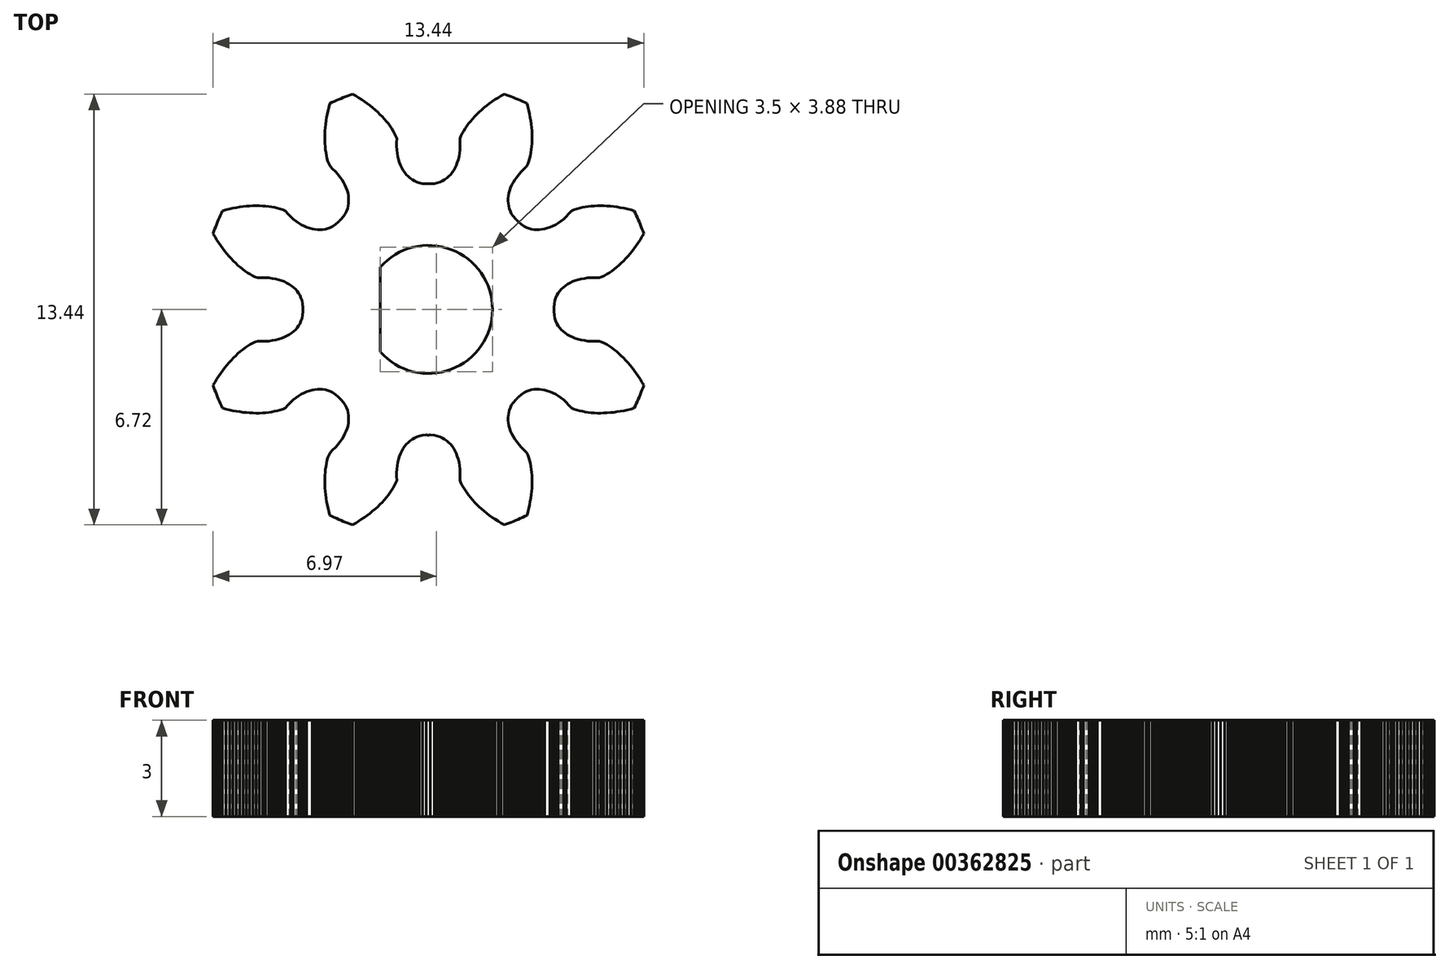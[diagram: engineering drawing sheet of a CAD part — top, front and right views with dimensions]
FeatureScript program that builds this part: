
annotation { "Feature Type Name" : "Feature", "Feature Type Description" : "" }
export const myFeature = defineFeature(function(context is Context, id is Id, definition is map)
    precondition{}
    {
        {
            var Q0;
            Q0=qCreatedBy(makeId("Top.planeOp"),FACE);
            var sketch = newSketch(context, id + "F0", { "sketchPlane" : qUnion([Q0])});
            skLineSegment(sketch, "E0", {"start": v(3.92, 0) * mm, "end": v(3.92, 0.01) * mm});
            skLineSegment(sketch, "E1", {"start": v(3.92, 0.01) * mm, "end": v(3.92, 0.03) * mm});
            skLineSegment(sketch, "E2", {"start": v(3.92, 0.03) * mm, "end": v(3.92, 0.04) * mm});
            skLineSegment(sketch, "E3", {"start": v(3.92, 0.04) * mm, "end": v(3.92, 0.05) * mm});
            skLineSegment(sketch, "E4", {"start": v(3.92, 0.05) * mm, "end": v(3.92, 0.06) * mm});
            skLineSegment(sketch, "E5", {"start": v(3.92, 0.06) * mm, "end": v(3.93, 0.18) * mm});
            skLineSegment(sketch, "E6", {"start": v(3.93, 0.18) * mm, "end": v(3.95, 0.28) * mm});
            skLineSegment(sketch, "E7", {"start": v(3.95, 0.28) * mm, "end": v(3.97, 0.36) * mm});
            skLineSegment(sketch, "E8", {"start": v(3.97, 0.36) * mm, "end": v(4, 0.44) * mm});
            skLineSegment(sketch, "E9", {"start": v(4, 0.44) * mm, "end": v(4.05, 0.5) * mm});
            skLineSegment(sketch, "E10", {"start": v(4.05, 0.5) * mm, "end": v(4.1, 0.57) * mm});
            skLineSegment(sketch, "E11", {"start": v(4.1, 0.57) * mm, "end": v(4.15, 0.63) * mm});
            skLineSegment(sketch, "E12", {"start": v(4.15, 0.63) * mm, "end": v(4.2, 0.69) * mm});
            skLineSegment(sketch, "E13", {"start": v(4.2, 0.69) * mm, "end": v(4.27, 0.74) * mm});
            skLineSegment(sketch, "E14", {"start": v(4.27, 0.74) * mm, "end": v(4.34, 0.79) * mm});
            skLineSegment(sketch, "E15", {"start": v(4.34, 0.79) * mm, "end": v(4.42, 0.83) * mm});
            skLineSegment(sketch, "E16", {"start": v(4.42, 0.83) * mm, "end": v(4.5, 0.87) * mm});
            skLineSegment(sketch, "E17", {"start": v(4.5, 0.87) * mm, "end": v(4.58, 0.9) * mm});
            skLineSegment(sketch, "E18", {"start": v(4.58, 0.9) * mm, "end": v(4.67, 0.93) * mm});
            skLineSegment(sketch, "E19", {"start": v(4.67, 0.93) * mm, "end": v(4.77, 0.96) * mm});
            skLineSegment(sketch, "E20", {"start": v(4.77, 0.96) * mm, "end": v(4.87, 0.97) * mm});
            skLineSegment(sketch, "E21", {"start": v(4.87, 0.97) * mm, "end": v(4.98, 0.99) * mm});
            skLineSegment(sketch, "E22", {"start": v(4.98, 0.99) * mm, "end": v(5.1, 1) * mm});
            skLineSegment(sketch, "E23", {"start": v(5.1, 1) * mm, "end": v(5.2, 0.99) * mm});
            skLineSegment(sketch, "E24", {"start": v(5.2, 0.99) * mm, "end": v(5.33, 0.99) * mm});
            skLineSegment(sketch, "E25", {"start": v(5.33, 0.99) * mm, "end": v(5.41, 1.02) * mm});
            skLineSegment(sketch, "E26", {"start": v(5.41, 1.02) * mm, "end": v(5.49, 1.06) * mm});
            skLineSegment(sketch, "E27", {"start": v(5.49, 1.06) * mm, "end": v(5.57, 1.1) * mm});
            skLineSegment(sketch, "E28", {"start": v(5.57, 1.1) * mm, "end": v(5.65, 1.15) * mm});
            skLineSegment(sketch, "E29", {"start": v(5.65, 1.15) * mm, "end": v(5.72, 1.2) * mm});
            skLineSegment(sketch, "E30", {"start": v(5.72, 1.2) * mm, "end": v(5.8, 1.25) * mm});
            skLineSegment(sketch, "E31", {"start": v(5.8, 1.25) * mm, "end": v(5.87, 1.31) * mm});
            skLineSegment(sketch, "E32", {"start": v(5.87, 1.31) * mm, "end": v(5.94, 1.38) * mm});
            skLineSegment(sketch, "E33", {"start": v(5.94, 1.38) * mm, "end": v(6.02, 1.44) * mm});
            skLineSegment(sketch, "E34", {"start": v(6.02, 1.44) * mm, "end": v(6.09, 1.51) * mm});
            skLineSegment(sketch, "E35", {"start": v(6.09, 1.51) * mm, "end": v(6.16, 1.58) * mm});
            skLineSegment(sketch, "E36", {"start": v(6.16, 1.58) * mm, "end": v(6.23, 1.66) * mm});
            skLineSegment(sketch, "E37", {"start": v(6.23, 1.66) * mm, "end": v(6.3, 1.74) * mm});
            skLineSegment(sketch, "E38", {"start": v(6.3, 1.74) * mm, "end": v(6.36, 1.82) * mm});
            skLineSegment(sketch, "E39", {"start": v(6.36, 1.82) * mm, "end": v(6.42, 1.9) * mm});
            skLineSegment(sketch, "E40", {"start": v(6.42, 1.9) * mm, "end": v(6.48, 2) * mm});
            skLineSegment(sketch, "E41", {"start": v(6.48, 2) * mm, "end": v(6.55, 2.08) * mm});
            skLineSegment(sketch, "E42", {"start": v(6.55, 2.08) * mm, "end": v(6.6, 2.17) * mm});
            skLineSegment(sketch, "E43", {"start": v(6.6, 2.17) * mm, "end": v(6.66, 2.27) * mm});
            skLineSegment(sketch, "E44", {"start": v(6.66, 2.27) * mm, "end": v(6.72, 2.37) * mm});
            skLineSegment(sketch, "E45", {"start": v(6.72, 2.37) * mm, "end": v(6.7, 2.44) * mm});
            skLineSegment(sketch, "E46", {"start": v(6.7, 2.44) * mm, "end": v(6.67, 2.51) * mm});
            skLineSegment(sketch, "E47", {"start": v(6.67, 2.51) * mm, "end": v(6.64, 2.58) * mm});
            skLineSegment(sketch, "E48", {"start": v(6.64, 2.58) * mm, "end": v(6.61, 2.66) * mm});
            skLineSegment(sketch, "E49", {"start": v(6.61, 2.66) * mm, "end": v(6.58, 2.73) * mm});
            skPoint(sketch, "E50", {"position": v(0, 5.7) * mm});
            skPoint(sketch, "E51", {"position": v(5.7, 0) * mm});
            skPoint(sketch, "E52", {"position": v(0, 0) * mm});
            skPoint(sketch, "E53", {"position": v(0, -5.7) * mm});
            skCircle(sketch, "E54", {"center": v(0, 0) * mm, "radius": 5.7 * mm, "construction": true});
            skLineSegment(sketch, "E55", {"start": v(5.7, 0) * mm, "end": v(-5.7, 0) * mm, "construction": true});
            skLineSegment(sketch, "E56", {"start": v(0, 5.7) * mm, "end": v(0, -5.7) * mm, "construction": true});
            skLineSegment(sketch, "E57.MirrorCS", {"start": v(3.92, 0) * mm, "end": v(3.92, -0.01) * mm});
            skLineSegment(sketch, "E58.MirrorCS", {"start": v(3.92, -0.03) * mm, "end": v(3.92, -0.04) * mm});
            skLineSegment(sketch, "E59.MirrorCS", {"start": v(3.92, -0.05) * mm, "end": v(3.92, -0.06) * mm});
            skLineSegment(sketch, "E60.MirrorCS", {"start": v(3.92, -0.01) * mm, "end": v(3.92, -0.03) * mm});
            skLineSegment(sketch, "E61.MirrorCS", {"start": v(3.92, -0.04) * mm, "end": v(3.92, -0.05) * mm});
            skLineSegment(sketch, "E62.MirrorCS", {"start": v(6.09, -1.51) * mm, "end": v(6.16, -1.58) * mm});
            skLineSegment(sketch, "E63.MirrorCS", {"start": v(4.67, -0.93) * mm, "end": v(4.77, -0.96) * mm});
            skLineSegment(sketch, "E64.MirrorCS", {"start": v(4.2, -0.69) * mm, "end": v(4.27, -0.74) * mm});
            skLineSegment(sketch, "E65.MirrorCS", {"start": v(4.27, -0.74) * mm, "end": v(4.34, -0.79) * mm});
            skLineSegment(sketch, "E66.MirrorCS", {"start": v(4.34, -0.79) * mm, "end": v(4.42, -0.83) * mm});
            skLineSegment(sketch, "E67.MirrorCS", {"start": v(3.92, -0.06) * mm, "end": v(3.93, -0.18) * mm});
            skLineSegment(sketch, "E68.MirrorCS", {"start": v(3.93, -0.18) * mm, "end": v(3.95, -0.28) * mm});
            skLineSegment(sketch, "E69.MirrorCS", {"start": v(3.95, -0.28) * mm, "end": v(3.97, -0.36) * mm});
            skLineSegment(sketch, "E70.MirrorCS", {"start": v(6.02, -1.44) * mm, "end": v(6.09, -1.51) * mm});
            skLineSegment(sketch, "E71.MirrorCS", {"start": v(3.97, -0.36) * mm, "end": v(4, -0.44) * mm});
            skLineSegment(sketch, "E72.MirrorCS", {"start": v(4, -0.44) * mm, "end": v(4.05, -0.5) * mm});
            skLineSegment(sketch, "E73.MirrorCS", {"start": v(4.05, -0.5) * mm, "end": v(4.1, -0.57) * mm});
            skLineSegment(sketch, "E74.MirrorCS", {"start": v(4.1, -0.57) * mm, "end": v(4.15, -0.63) * mm});
            skLineSegment(sketch, "E75.MirrorCS", {"start": v(4.15, -0.63) * mm, "end": v(4.2, -0.69) * mm});
            skLineSegment(sketch, "E76.MirrorCS", {"start": v(5.49, -1.06) * mm, "end": v(5.57, -1.1) * mm});
            skLineSegment(sketch, "E77.MirrorCS", {"start": v(6.6, -2.17) * mm, "end": v(6.66, -2.27) * mm});
            skLineSegment(sketch, "E78.MirrorCS", {"start": v(6.36, -1.82) * mm, "end": v(6.42, -1.9) * mm});
            skLineSegment(sketch, "E79.MirrorCS", {"start": v(5.1, -1) * mm, "end": v(5.2, -0.99) * mm});
            skLineSegment(sketch, "E80.MirrorCS", {"start": v(4.77, -0.96) * mm, "end": v(4.87, -0.97) * mm});
            skLineSegment(sketch, "E81.MirrorCS", {"start": v(6.72, -2.37) * mm, "end": v(6.7, -2.44) * mm});
            skLineSegment(sketch, "E82.MirrorCS", {"start": v(5.41, -1.02) * mm, "end": v(5.49, -1.06) * mm});
            skLineSegment(sketch, "E83.MirrorCS", {"start": v(5.65, -1.15) * mm, "end": v(5.72, -1.2) * mm});
            skLineSegment(sketch, "E84.MirrorCS", {"start": v(6.16, -1.58) * mm, "end": v(6.23, -1.66) * mm});
            skLineSegment(sketch, "E85.MirrorCS", {"start": v(4.42, -0.83) * mm, "end": v(4.5, -0.87) * mm});
            skLineSegment(sketch, "E86.MirrorCS", {"start": v(6.55, -2.08) * mm, "end": v(6.6, -2.17) * mm});
            skLineSegment(sketch, "E87.MirrorCS", {"start": v(6.64, -2.58) * mm, "end": v(6.61, -2.66) * mm});
            skLineSegment(sketch, "E88.MirrorCS", {"start": v(5.87, -1.31) * mm, "end": v(5.94, -1.38) * mm});
            skLineSegment(sketch, "E89.MirrorCS", {"start": v(6.66, -2.27) * mm, "end": v(6.72, -2.37) * mm});
            skLineSegment(sketch, "E90.MirrorCS", {"start": v(5.57, -1.1) * mm, "end": v(5.65, -1.15) * mm});
            skLineSegment(sketch, "E91.MirrorCS", {"start": v(6.42, -1.9) * mm, "end": v(6.48, -2) * mm});
            skLineSegment(sketch, "E92.MirrorCS", {"start": v(5.2, -0.99) * mm, "end": v(5.33, -0.99) * mm});
            skLineSegment(sketch, "E93.MirrorCS", {"start": v(4.87, -0.97) * mm, "end": v(4.98, -0.99) * mm});
            skLineSegment(sketch, "E94.MirrorCS", {"start": v(6.7, -2.44) * mm, "end": v(6.67, -2.51) * mm});
            skLineSegment(sketch, "E95.MirrorCS", {"start": v(5.72, -1.2) * mm, "end": v(5.8, -1.25) * mm});
            skLineSegment(sketch, "E96.MirrorCS", {"start": v(4.58, -0.9) * mm, "end": v(4.67, -0.93) * mm});
            skLineSegment(sketch, "E97.MirrorCS", {"start": v(6.23, -1.66) * mm, "end": v(6.3, -1.74) * mm});
            skLineSegment(sketch, "E98.MirrorCS", {"start": v(4.5, -0.87) * mm, "end": v(4.58, -0.9) * mm});
            skLineSegment(sketch, "E99.MirrorCS", {"start": v(6.61, -2.66) * mm, "end": v(6.58, -2.73) * mm});
            skLineSegment(sketch, "E100.MirrorCS", {"start": v(5.94, -1.38) * mm, "end": v(6.02, -1.44) * mm});
            skLineSegment(sketch, "E101.MirrorCS", {"start": v(6.48, -2) * mm, "end": v(6.55, -2.08) * mm});
            skLineSegment(sketch, "E102.MirrorCS", {"start": v(5.33, -0.99) * mm, "end": v(5.41, -1.02) * mm});
            skLineSegment(sketch, "E103.MirrorCS", {"start": v(6.67, -2.51) * mm, "end": v(6.64, -2.58) * mm});
            skLineSegment(sketch, "E104.MirrorCS", {"start": v(4.98, -0.99) * mm, "end": v(5.1, -1) * mm});
            skLineSegment(sketch, "E105.MirrorCS", {"start": v(6.3, -1.74) * mm, "end": v(6.36, -1.82) * mm});
            skLineSegment(sketch, "E106.MirrorCS", {"start": v(5.8, -1.25) * mm, "end": v(5.87, -1.31) * mm});
            skPoint(sketch, "E107.1.0", {"position": v(4.03, 4.03) * mm});
            skPoint(sketch, "E107.1.1", {"position": v(4.03, 4.03) * mm});
            skLineSegment(sketch, "E107.1.2", {"start": v(4.22, 2.82) * mm, "end": v(4.3, 2.9) * mm});
            skLineSegment(sketch, "E107.1.3", {"start": v(5.58, 3.23) * mm, "end": v(5.68, 3.22) * mm});
            skLineSegment(sketch, "E107.1.4", {"start": v(5.37, 3.23) * mm, "end": v(5.47, 3.23) * mm});
            skLineSegment(sketch, "E107.1.5", {"start": v(3.16, 6.1) * mm, "end": v(3.13, 6.2) * mm});
            skLineSegment(sketch, "E107.1.6", {"start": v(3.1, 4.54) * mm, "end": v(3.14, 4.63) * mm});
            skLineSegment(sketch, "E107.1.7", {"start": v(5.78, 3.2) * mm, "end": v(5.89, 3.2) * mm});
            skLineSegment(sketch, "E107.1.8", {"start": v(2.65, 3.96) * mm, "end": v(2.7, 4.05) * mm});
            skLineSegment(sketch, "E107.1.9", {"start": v(3.06, 2.56) * mm, "end": v(3.15, 2.52) * mm});
            skLineSegment(sketch, "E107.1.10", {"start": v(4.8, 3.18) * mm, "end": v(4.9, 3.2) * mm});
            skLineSegment(sketch, "E107.1.11", {"start": v(3.23, 5.37) * mm, "end": v(3.23, 5.47) * mm});
            skLineSegment(sketch, "E107.1.12", {"start": v(3.1, 6.32) * mm, "end": v(3.08, 6.43) * mm});
            skLineSegment(sketch, "E107.1.13", {"start": v(3.46, 2.49) * mm, "end": v(3.54, 2.5) * mm});
            skLineSegment(sketch, "E107.1.14", {"start": v(3.16, 4.71) * mm, "end": v(3.18, 4.8) * mm});
            skLineSegment(sketch, "E107.1.15", {"start": v(4.05, 2.7) * mm, "end": v(4.13, 2.76) * mm});
            skLineSegment(sketch, "E107.1.16", {"start": v(3.88, 2.6) * mm, "end": v(3.96, 2.65) * mm});
            skLineSegment(sketch, "E107.1.17", {"start": v(4.54, 3.1) * mm, "end": v(4.63, 3.14) * mm});
            skLineSegment(sketch, "E107.1.18", {"start": v(3.63, 2.51) * mm, "end": v(3.71, 2.54) * mm});
            skLineSegment(sketch, "E107.1.19", {"start": v(6.32, 3.1) * mm, "end": v(6.43, 3.08) * mm});
            skLineSegment(sketch, "E107.1.20", {"start": v(3.22, 2.5) * mm, "end": v(3.3, 2.5) * mm});
            skLineSegment(sketch, "E107.1.21", {"start": v(3.23, 5.58) * mm, "end": v(3.22, 5.68) * mm});
            skLineSegment(sketch, "E107.1.22", {"start": v(3.2, 4.9) * mm, "end": v(3.21, 4.99) * mm});
            skLineSegment(sketch, "E107.1.23", {"start": v(4.71, 3.16) * mm, "end": v(4.8, 3.18) * mm});
            skLineSegment(sketch, "E107.1.24", {"start": v(3.96, 2.65) * mm, "end": v(4.05, 2.7) * mm});
            skLineSegment(sketch, "E107.1.25", {"start": v(3.13, 6.2) * mm, "end": v(3.1, 6.32) * mm});
            skLineSegment(sketch, "E107.1.26", {"start": v(4.9, 3.2) * mm, "end": v(4.99, 3.21) * mm});
            skLineSegment(sketch, "E107.1.27", {"start": v(3.14, 4.63) * mm, "end": v(3.16, 4.71) * mm});
            skLineSegment(sketch, "E107.1.28", {"start": v(2.7, 4.05) * mm, "end": v(2.76, 4.13) * mm});
            skLineSegment(sketch, "E107.1.29", {"start": v(4.3, 2.9) * mm, "end": v(4.38, 2.98) * mm});
            skLineSegment(sketch, "E107.1.30", {"start": v(5.08, 3.22) * mm, "end": v(5.18, 3.23) * mm});
            skLineSegment(sketch, "E107.1.31", {"start": v(5.68, 3.22) * mm, "end": v(5.78, 3.2) * mm});
            skLineSegment(sketch, "E107.1.32", {"start": v(3.8, 2.57) * mm, "end": v(3.88, 2.6) * mm});
            skLineSegment(sketch, "E107.1.33", {"start": v(3.15, 2.52) * mm, "end": v(3.22, 2.5) * mm});
            skLineSegment(sketch, "E107.1.34", {"start": v(3.54, 2.5) * mm, "end": v(3.63, 2.51) * mm});
            skLineSegment(sketch, "E107.1.35", {"start": v(3.23, 5.47) * mm, "end": v(3.23, 5.58) * mm});
            skLineSegment(sketch, "E107.1.36", {"start": v(3.18, 4.8) * mm, "end": v(3.2, 4.9) * mm});
            skLineSegment(sketch, "E107.1.37", {"start": v(3.3, 2.5) * mm, "end": v(3.38, 2.49) * mm});
            skLineSegment(sketch, "E107.1.38", {"start": v(3.22, 5.68) * mm, "end": v(3.2, 5.78) * mm});
            skLineSegment(sketch, "E107.1.39", {"start": v(3.21, 4.99) * mm, "end": v(3.22, 5.08) * mm});
            skLineSegment(sketch, "E107.1.40", {"start": v(4.99, 3.21) * mm, "end": v(5.08, 3.22) * mm});
            skLineSegment(sketch, "E107.1.41", {"start": v(6.55, 2.8) * mm, "end": v(6.58, 2.73) * mm});
            skLineSegment(sketch, "E107.1.42", {"start": v(2.49, 3.46) * mm, "end": v(2.5, 3.54) * mm});
            skLineSegment(sketch, "E107.1.43", {"start": v(2.5, 3.54) * mm, "end": v(2.51, 3.63) * mm});
            skLineSegment(sketch, "E107.1.44", {"start": v(2.51, 3.63) * mm, "end": v(2.54, 3.71) * mm});
            skLineSegment(sketch, "E107.1.45", {"start": v(2.65, 2.9) * mm, "end": v(2.6, 2.99) * mm});
            skLineSegment(sketch, "E107.1.46", {"start": v(2.6, 2.99) * mm, "end": v(2.56, 3.06) * mm});
            skLineSegment(sketch, "E107.1.47", {"start": v(2.56, 3.06) * mm, "end": v(2.52, 3.15) * mm});
            skLineSegment(sketch, "E107.1.48", {"start": v(2.52, 3.15) * mm, "end": v(2.5, 3.22) * mm});
            skLineSegment(sketch, "E107.1.49", {"start": v(2.5, 3.22) * mm, "end": v(2.5, 3.3) * mm});
            skLineSegment(sketch, "E107.1.50", {"start": v(2.5, 3.3) * mm, "end": v(2.49, 3.38) * mm});
            skLineSegment(sketch, "E107.1.51", {"start": v(2.49, 3.38) * mm, "end": v(2.49, 3.46) * mm});
            skLineSegment(sketch, "E107.1.52", {"start": v(5.18, 3.23) * mm, "end": v(5.27, 3.23) * mm});
            skLineSegment(sketch, "E107.1.53", {"start": v(3.2, 5.78) * mm, "end": v(3.2, 5.89) * mm});
            skLineSegment(sketch, "E107.1.54", {"start": v(5.89, 3.2) * mm, "end": v(6, 3.18) * mm});
            skLineSegment(sketch, "E107.1.55", {"start": v(3.38, 2.49) * mm, "end": v(3.46, 2.49) * mm});
            skLineSegment(sketch, "E107.1.56", {"start": v(2.54, 3.71) * mm, "end": v(2.57, 3.8) * mm});
            skLineSegment(sketch, "E107.1.57", {"start": v(5.47, 3.23) * mm, "end": v(5.58, 3.23) * mm});
            skLineSegment(sketch, "E107.1.58", {"start": v(3.22, 5.08) * mm, "end": v(3.23, 5.18) * mm});
            skLineSegment(sketch, "E107.1.59", {"start": v(3.2, 5.89) * mm, "end": v(3.18, 6) * mm});
            skLineSegment(sketch, "E107.1.60", {"start": v(2.98, 4.38) * mm, "end": v(3.07, 4.47) * mm});
            skLineSegment(sketch, "E107.1.61", {"start": v(4.38, 2.98) * mm, "end": v(4.47, 3.07) * mm});
            skLineSegment(sketch, "E107.1.62", {"start": v(4.63, 3.14) * mm, "end": v(4.71, 3.16) * mm});
            skLineSegment(sketch, "E107.1.63", {"start": v(2.57, 3.8) * mm, "end": v(2.6, 3.88) * mm});
            skLineSegment(sketch, "E107.1.64", {"start": v(3.71, 2.54) * mm, "end": v(3.8, 2.57) * mm});
            skLineSegment(sketch, "E107.1.65", {"start": v(3.23, 5.18) * mm, "end": v(3.23, 5.27) * mm});
            skLineSegment(sketch, "E107.1.66", {"start": v(6, 3.18) * mm, "end": v(6.1, 3.16) * mm});
            skLineSegment(sketch, "E107.1.67", {"start": v(3.18, 6) * mm, "end": v(3.16, 6.1) * mm});
            skLineSegment(sketch, "E107.1.68", {"start": v(3.07, 4.47) * mm, "end": v(3.1, 4.54) * mm});
            skLineSegment(sketch, "E107.1.69", {"start": v(4.13, 2.76) * mm, "end": v(4.22, 2.82) * mm});
            skLineSegment(sketch, "E107.1.70", {"start": v(6.2, 3.13) * mm, "end": v(6.32, 3.1) * mm});
            skLineSegment(sketch, "E107.1.71", {"start": v(2.6, 3.88) * mm, "end": v(2.65, 3.96) * mm});
            skLineSegment(sketch, "E107.1.72", {"start": v(6.1, 3.16) * mm, "end": v(6.2, 3.13) * mm});
            skLineSegment(sketch, "E107.1.73", {"start": v(5.27, 3.23) * mm, "end": v(5.37, 3.23) * mm});
            skLineSegment(sketch, "E107.1.74", {"start": v(3.23, 5.27) * mm, "end": v(3.23, 5.37) * mm});
            skLineSegment(sketch, "E107.1.75", {"start": v(4.47, 3.07) * mm, "end": v(4.54, 3.1) * mm});
            skLineSegment(sketch, "E107.1.76", {"start": v(2.76, 4.13) * mm, "end": v(2.82, 4.22) * mm});
            skLineSegment(sketch, "E107.1.77", {"start": v(2.82, 4.22) * mm, "end": v(2.9, 4.3) * mm});
            skLineSegment(sketch, "E107.1.78", {"start": v(2.9, 4.3) * mm, "end": v(2.98, 4.38) * mm});
            skLineSegment(sketch, "E107.1.79", {"start": v(2.8, 6.55) * mm, "end": v(2.73, 6.58) * mm});
            skLineSegment(sketch, "E107.1.80", {"start": v(6.46, 3) * mm, "end": v(6.5, 2.94) * mm});
            skLineSegment(sketch, "E107.1.81", {"start": v(6.52, 2.87) * mm, "end": v(6.55, 2.8) * mm});
            skLineSegment(sketch, "E107.1.82", {"start": v(6.5, 2.94) * mm, "end": v(6.52, 2.87) * mm});
            skLineSegment(sketch, "E107.1.83", {"start": v(3, 6.46) * mm, "end": v(2.94, 6.5) * mm});
            skLineSegment(sketch, "E107.1.84", {"start": v(6.43, 3.08) * mm, "end": v(6.46, 3) * mm});
            skLineSegment(sketch, "E107.1.85", {"start": v(3.08, 6.43) * mm, "end": v(3, 6.46) * mm});
            skLineSegment(sketch, "E107.1.86", {"start": v(2.94, 6.5) * mm, "end": v(2.87, 6.52) * mm});
            skLineSegment(sketch, "E107.1.87", {"start": v(2.9, 2.65) * mm, "end": v(2.99, 2.6) * mm});
            skLineSegment(sketch, "E107.1.88", {"start": v(2.87, 6.52) * mm, "end": v(2.8, 6.55) * mm});
            skLineSegment(sketch, "E107.1.89", {"start": v(2.99, 2.6) * mm, "end": v(3.06, 2.56) * mm});
            skLineSegment(sketch, "E107.1.90", {"start": v(2.82, 2.73) * mm, "end": v(2.9, 2.65) * mm});
            skLineSegment(sketch, "E107.1.91", {"start": v(2.79, 2.75) * mm, "end": v(2.8, 2.74) * mm});
            skLineSegment(sketch, "E107.1.92", {"start": v(2.76, 2.78) * mm, "end": v(2.75, 2.79) * mm});
            skLineSegment(sketch, "E107.1.93", {"start": v(2.73, 2.82) * mm, "end": v(2.65, 2.9) * mm});
            skLineSegment(sketch, "E107.1.94", {"start": v(2.74, 2.8) * mm, "end": v(2.73, 2.82) * mm});
            skLineSegment(sketch, "E107.1.95", {"start": v(2.74, 2.8) * mm, "end": v(2.74, 2.8) * mm});
            skLineSegment(sketch, "E107.1.96", {"start": v(2.75, 2.79) * mm, "end": v(2.74, 2.8) * mm});
            skLineSegment(sketch, "E107.1.97", {"start": v(2.77, 2.77) * mm, "end": v(2.76, 2.78) * mm});
            skLineSegment(sketch, "E107.1.98", {"start": v(2.77, 2.77) * mm, "end": v(2.78, 2.76) * mm});
            skLineSegment(sketch, "E107.1.99", {"start": v(2.78, 2.76) * mm, "end": v(2.79, 2.75) * mm});
            skLineSegment(sketch, "E107.1.100", {"start": v(2.8, 2.74) * mm, "end": v(2.8, 2.74) * mm});
            skLineSegment(sketch, "E107.1.101", {"start": v(2.8, 2.74) * mm, "end": v(2.82, 2.73) * mm});
            skLineSegment(sketch, "E107.2.2", {"start": v(0.99, 4.98) * mm, "end": v(1, 5.1) * mm});
            skLineSegment(sketch, "E107.2.3", {"start": v(1.66, 6.23) * mm, "end": v(1.74, 6.3) * mm});
            skLineSegment(sketch, "E107.2.4", {"start": v(1.51, 6.09) * mm, "end": v(1.58, 6.16) * mm});
            skLineSegment(sketch, "E107.2.5", {"start": v(-2.08, 6.55) * mm, "end": v(-2.17, 6.6) * mm});
            skLineSegment(sketch, "E107.2.6", {"start": v(-1.02, 5.41) * mm, "end": v(-1.06, 5.49) * mm});
            skLineSegment(sketch, "E107.2.7", {"start": v(1.82, 6.36) * mm, "end": v(1.9, 6.42) * mm});
            skLineSegment(sketch, "E107.2.8", {"start": v(-0.93, 4.67) * mm, "end": v(-0.96, 4.77) * mm});
            skLineSegment(sketch, "E107.2.9", {"start": v(0.36, 3.97) * mm, "end": v(0.44, 4) * mm});
            skLineSegment(sketch, "E107.2.10", {"start": v(1.15, 5.65) * mm, "end": v(1.2, 5.72) * mm});
            skLineSegment(sketch, "E107.2.11", {"start": v(-1.51, 6.09) * mm, "end": v(-1.58, 6.16) * mm});
            skLineSegment(sketch, "E107.2.12", {"start": v(-2.27, 6.66) * mm, "end": v(-2.37, 6.72) * mm});
            skLineSegment(sketch, "E107.2.13", {"start": v(0.69, 4.2) * mm, "end": v(0.74, 4.27) * mm});
            skLineSegment(sketch, "E107.2.14", {"start": v(-1.1, 5.57) * mm, "end": v(-1.15, 5.65) * mm});
            skLineSegment(sketch, "E107.2.15", {"start": v(0.96, 4.77) * mm, "end": v(0.97, 4.87) * mm});
            skLineSegment(sketch, "E107.2.16", {"start": v(0.9, 4.58) * mm, "end": v(0.93, 4.67) * mm});
            skLineSegment(sketch, "E107.2.17", {"start": v(1.02, 5.41) * mm, "end": v(1.06, 5.49) * mm});
            skLineSegment(sketch, "E107.2.18", {"start": v(0.79, 4.34) * mm, "end": v(0.83, 4.42) * mm});
            skLineSegment(sketch, "E107.2.19", {"start": v(2.27, 6.66) * mm, "end": v(2.37, 6.72) * mm});
            skLineSegment(sketch, "E107.2.20", {"start": v(0.5, 4.05) * mm, "end": v(0.57, 4.1) * mm});
            skLineSegment(sketch, "E107.2.21", {"start": v(-1.66, 6.23) * mm, "end": v(-1.74, 6.3) * mm});
            skLineSegment(sketch, "E107.2.22", {"start": v(-1.2, 5.72) * mm, "end": v(-1.25, 5.8) * mm});
            skLineSegment(sketch, "E107.2.23", {"start": v(1.1, 5.57) * mm, "end": v(1.15, 5.65) * mm});
            skLineSegment(sketch, "E107.2.24", {"start": v(0.93, 4.67) * mm, "end": v(0.96, 4.77) * mm});
            skLineSegment(sketch, "E107.2.25", {"start": v(-2.17, 6.6) * mm, "end": v(-2.27, 6.66) * mm});
            skLineSegment(sketch, "E107.2.26", {"start": v(1.2, 5.72) * mm, "end": v(1.25, 5.8) * mm});
            skLineSegment(sketch, "E107.2.27", {"start": v(-1.06, 5.49) * mm, "end": v(-1.1, 5.57) * mm});
            skLineSegment(sketch, "E107.2.28", {"start": v(-0.96, 4.77) * mm, "end": v(-0.97, 4.87) * mm});
            skLineSegment(sketch, "E107.2.29", {"start": v(1, 5.1) * mm, "end": v(0.99, 5.2) * mm});
            skLineSegment(sketch, "E107.2.30", {"start": v(1.31, 5.87) * mm, "end": v(1.38, 5.94) * mm});
            skLineSegment(sketch, "E107.2.31", {"start": v(1.74, 6.3) * mm, "end": v(1.82, 6.36) * mm});
            skLineSegment(sketch, "E107.2.32", {"start": v(0.87, 4.5) * mm, "end": v(0.9, 4.58) * mm});
            skLineSegment(sketch, "E107.2.33", {"start": v(0.44, 4) * mm, "end": v(0.5, 4.05) * mm});
            skLineSegment(sketch, "E107.2.34", {"start": v(0.74, 4.27) * mm, "end": v(0.79, 4.34) * mm});
            skLineSegment(sketch, "E107.2.35", {"start": v(-1.58, 6.16) * mm, "end": v(-1.66, 6.23) * mm});
            skLineSegment(sketch, "E107.2.36", {"start": v(-1.15, 5.65) * mm, "end": v(-1.2, 5.72) * mm});
            skLineSegment(sketch, "E107.2.37", {"start": v(0.57, 4.1) * mm, "end": v(0.63, 4.15) * mm});
            skLineSegment(sketch, "E107.2.38", {"start": v(-1.74, 6.3) * mm, "end": v(-1.82, 6.36) * mm});
            skLineSegment(sketch, "E107.2.39", {"start": v(-1.25, 5.8) * mm, "end": v(-1.31, 5.87) * mm});
            skLineSegment(sketch, "E107.2.40", {"start": v(1.25, 5.8) * mm, "end": v(1.31, 5.87) * mm});
            skLineSegment(sketch, "E107.2.41", {"start": v(2.66, 6.61) * mm, "end": v(2.73, 6.58) * mm});
            skLineSegment(sketch, "E107.2.42", {"start": v(-0.69, 4.2) * mm, "end": v(-0.74, 4.27) * mm});
            skLineSegment(sketch, "E107.2.43", {"start": v(-0.74, 4.27) * mm, "end": v(-0.79, 4.34) * mm});
            skLineSegment(sketch, "E107.2.44", {"start": v(-0.79, 4.34) * mm, "end": v(-0.83, 4.42) * mm});
            skLineSegment(sketch, "E107.2.45", {"start": v(-0.18, 3.93) * mm, "end": v(-0.28, 3.95) * mm});
            skLineSegment(sketch, "E107.2.46", {"start": v(-0.28, 3.95) * mm, "end": v(-0.36, 3.97) * mm});
            skLineSegment(sketch, "E107.2.47", {"start": v(-0.36, 3.97) * mm, "end": v(-0.44, 4) * mm});
            skLineSegment(sketch, "E107.2.48", {"start": v(-0.44, 4) * mm, "end": v(-0.5, 4.05) * mm});
            skLineSegment(sketch, "E107.2.49", {"start": v(-0.5, 4.05) * mm, "end": v(-0.57, 4.1) * mm});
            skLineSegment(sketch, "E107.2.50", {"start": v(-0.57, 4.1) * mm, "end": v(-0.63, 4.15) * mm});
            skLineSegment(sketch, "E107.2.51", {"start": v(-0.63, 4.15) * mm, "end": v(-0.69, 4.2) * mm});
            skLineSegment(sketch, "E107.2.52", {"start": v(1.38, 5.94) * mm, "end": v(1.44, 6.02) * mm});
            skLineSegment(sketch, "E107.2.53", {"start": v(-1.82, 6.36) * mm, "end": v(-1.9, 6.42) * mm});
            skLineSegment(sketch, "E107.2.54", {"start": v(1.9, 6.42) * mm, "end": v(2, 6.48) * mm});
            skLineSegment(sketch, "E107.2.55", {"start": v(0.63, 4.15) * mm, "end": v(0.69, 4.2) * mm});
            skLineSegment(sketch, "E107.2.56", {"start": v(-0.83, 4.42) * mm, "end": v(-0.87, 4.5) * mm});
            skLineSegment(sketch, "E107.2.57", {"start": v(1.58, 6.16) * mm, "end": v(1.66, 6.23) * mm});
            skLineSegment(sketch, "E107.2.58", {"start": v(-1.31, 5.87) * mm, "end": v(-1.38, 5.94) * mm});
            skLineSegment(sketch, "E107.2.59", {"start": v(-1.9, 6.42) * mm, "end": v(-2, 6.48) * mm});
            skLineSegment(sketch, "E107.2.60", {"start": v(-0.99, 5.2) * mm, "end": v(-0.99, 5.33) * mm});
            skLineSegment(sketch, "E107.2.61", {"start": v(0.99, 5.2) * mm, "end": v(0.99, 5.33) * mm});
            skLineSegment(sketch, "E107.2.62", {"start": v(1.06, 5.49) * mm, "end": v(1.1, 5.57) * mm});
            skLineSegment(sketch, "E107.2.63", {"start": v(-0.87, 4.5) * mm, "end": v(-0.9, 4.58) * mm});
            skLineSegment(sketch, "E107.2.64", {"start": v(0.83, 4.42) * mm, "end": v(0.87, 4.5) * mm});
            skLineSegment(sketch, "E107.2.65", {"start": v(-1.38, 5.94) * mm, "end": v(-1.44, 6.02) * mm});
            skLineSegment(sketch, "E107.2.66", {"start": v(2, 6.48) * mm, "end": v(2.08, 6.55) * mm});
            skLineSegment(sketch, "E107.2.67", {"start": v(-2, 6.48) * mm, "end": v(-2.08, 6.55) * mm});
            skLineSegment(sketch, "E107.2.68", {"start": v(-0.99, 5.33) * mm, "end": v(-1.02, 5.41) * mm});
            skLineSegment(sketch, "E107.2.69", {"start": v(0.97, 4.87) * mm, "end": v(0.99, 4.98) * mm});
            skLineSegment(sketch, "E107.2.70", {"start": v(2.17, 6.6) * mm, "end": v(2.27, 6.66) * mm});
            skLineSegment(sketch, "E107.2.71", {"start": v(-0.9, 4.58) * mm, "end": v(-0.93, 4.67) * mm});
            skLineSegment(sketch, "E107.2.72", {"start": v(2.08, 6.55) * mm, "end": v(2.17, 6.6) * mm});
            skLineSegment(sketch, "E107.2.73", {"start": v(1.44, 6.02) * mm, "end": v(1.51, 6.09) * mm});
            skLineSegment(sketch, "E107.2.74", {"start": v(-1.44, 6.02) * mm, "end": v(-1.51, 6.09) * mm});
            skLineSegment(sketch, "E107.2.75", {"start": v(0.99, 5.33) * mm, "end": v(1.02, 5.41) * mm});
            skLineSegment(sketch, "E107.2.76", {"start": v(-0.97, 4.87) * mm, "end": v(-0.99, 4.98) * mm});
            skLineSegment(sketch, "E107.2.77", {"start": v(-0.99, 4.98) * mm, "end": v(-1, 5.1) * mm});
            skLineSegment(sketch, "E107.2.78", {"start": v(-1, 5.1) * mm, "end": v(-0.99, 5.2) * mm});
            skLineSegment(sketch, "E107.2.79", {"start": v(-2.66, 6.61) * mm, "end": v(-2.73, 6.58) * mm});
            skLineSegment(sketch, "E107.2.80", {"start": v(2.44, 6.7) * mm, "end": v(2.51, 6.67) * mm});
            skLineSegment(sketch, "E107.2.81", {"start": v(2.58, 6.64) * mm, "end": v(2.66, 6.61) * mm});
            skLineSegment(sketch, "E107.2.82", {"start": v(2.51, 6.67) * mm, "end": v(2.58, 6.64) * mm});
            skLineSegment(sketch, "E107.2.83", {"start": v(-2.44, 6.7) * mm, "end": v(-2.51, 6.67) * mm});
            skLineSegment(sketch, "E107.2.84", {"start": v(2.37, 6.72) * mm, "end": v(2.44, 6.7) * mm});
            skLineSegment(sketch, "E107.2.85", {"start": v(-2.37, 6.72) * mm, "end": v(-2.44, 6.7) * mm});
            skLineSegment(sketch, "E107.2.86", {"start": v(-2.51, 6.67) * mm, "end": v(-2.58, 6.64) * mm});
            skLineSegment(sketch, "E107.2.87", {"start": v(0.18, 3.93) * mm, "end": v(0.28, 3.95) * mm});
            skLineSegment(sketch, "E107.2.88", {"start": v(-2.58, 6.64) * mm, "end": v(-2.66, 6.61) * mm});
            skLineSegment(sketch, "E107.2.89", {"start": v(0.28, 3.95) * mm, "end": v(0.36, 3.97) * mm});
            skLineSegment(sketch, "E107.2.90", {"start": v(0.06, 3.92) * mm, "end": v(0.18, 3.93) * mm});
            skLineSegment(sketch, "E107.2.91", {"start": v(0.03, 3.92) * mm, "end": v(0.04, 3.92) * mm});
            skLineSegment(sketch, "E107.2.92", {"start": v(-0.01, 3.92) * mm, "end": v(-0.03, 3.92) * mm});
            skLineSegment(sketch, "E107.2.93", {"start": v(-0.06, 3.92) * mm, "end": v(-0.18, 3.93) * mm});
            skLineSegment(sketch, "E107.2.94", {"start": v(-0.05, 3.92) * mm, "end": v(-0.06, 3.92) * mm});
            skLineSegment(sketch, "E107.2.95", {"start": v(-0.04, 3.92) * mm, "end": v(-0.05, 3.92) * mm});
            skLineSegment(sketch, "E107.2.96", {"start": v(-0.03, 3.92) * mm, "end": v(-0.04, 3.92) * mm});
            skLineSegment(sketch, "E107.2.97", {"start": v(0, 3.92) * mm, "end": v(-0.01, 3.92) * mm});
            skLineSegment(sketch, "E107.2.98", {"start": v(0, 3.92) * mm, "end": v(0.01, 3.92) * mm});
            skLineSegment(sketch, "E107.2.99", {"start": v(0.01, 3.92) * mm, "end": v(0.03, 3.92) * mm});
            skLineSegment(sketch, "E107.2.100", {"start": v(0.04, 3.92) * mm, "end": v(0.05, 3.92) * mm});
            skLineSegment(sketch, "E107.2.101", {"start": v(0.05, 3.92) * mm, "end": v(0.06, 3.92) * mm});
            skPoint(sketch, "E107.3.0", {"position": v(-4.03, 4.03) * mm});
            skPoint(sketch, "E107.3.1", {"position": v(-4.03, 4.03) * mm});
            skLineSegment(sketch, "E107.3.2", {"start": v(-2.82, 4.22) * mm, "end": v(-2.9, 4.3) * mm});
            skLineSegment(sketch, "E107.3.3", {"start": v(-3.23, 5.58) * mm, "end": v(-3.22, 5.68) * mm});
            skLineSegment(sketch, "E107.3.4", {"start": v(-3.23, 5.37) * mm, "end": v(-3.23, 5.47) * mm});
            skLineSegment(sketch, "E107.3.5", {"start": v(-6.1, 3.16) * mm, "end": v(-6.2, 3.13) * mm});
            skLineSegment(sketch, "E107.3.6", {"start": v(-4.54, 3.1) * mm, "end": v(-4.63, 3.14) * mm});
            skLineSegment(sketch, "E107.3.7", {"start": v(-3.2, 5.78) * mm, "end": v(-3.2, 5.89) * mm});
            skLineSegment(sketch, "E107.3.8", {"start": v(-3.96, 2.65) * mm, "end": v(-4.05, 2.7) * mm});
            skLineSegment(sketch, "E107.3.9", {"start": v(-2.56, 3.06) * mm, "end": v(-2.52, 3.15) * mm});
            skLineSegment(sketch, "E107.3.10", {"start": v(-3.18, 4.8) * mm, "end": v(-3.2, 4.9) * mm});
            skLineSegment(sketch, "E107.3.11", {"start": v(-5.37, 3.23) * mm, "end": v(-5.47, 3.23) * mm});
            skLineSegment(sketch, "E107.3.12", {"start": v(-6.32, 3.1) * mm, "end": v(-6.43, 3.08) * mm});
            skLineSegment(sketch, "E107.3.13", {"start": v(-2.49, 3.46) * mm, "end": v(-2.5, 3.54) * mm});
            skLineSegment(sketch, "E107.3.14", {"start": v(-4.71, 3.16) * mm, "end": v(-4.8, 3.18) * mm});
            skLineSegment(sketch, "E107.3.15", {"start": v(-2.7, 4.05) * mm, "end": v(-2.76, 4.13) * mm});
            skLineSegment(sketch, "E107.3.16", {"start": v(-2.6, 3.88) * mm, "end": v(-2.65, 3.96) * mm});
            skLineSegment(sketch, "E107.3.17", {"start": v(-3.1, 4.54) * mm, "end": v(-3.14, 4.63) * mm});
            skLineSegment(sketch, "E107.3.18", {"start": v(-2.51, 3.63) * mm, "end": v(-2.54, 3.71) * mm});
            skLineSegment(sketch, "E107.3.19", {"start": v(-3.1, 6.32) * mm, "end": v(-3.08, 6.43) * mm});
            skLineSegment(sketch, "E107.3.20", {"start": v(-2.5, 3.22) * mm, "end": v(-2.5, 3.3) * mm});
            skLineSegment(sketch, "E107.3.21", {"start": v(-5.58, 3.23) * mm, "end": v(-5.68, 3.22) * mm});
            skLineSegment(sketch, "E107.3.22", {"start": v(-4.9, 3.2) * mm, "end": v(-4.99, 3.21) * mm});
            skLineSegment(sketch, "E107.3.23", {"start": v(-3.16, 4.71) * mm, "end": v(-3.18, 4.8) * mm});
            skLineSegment(sketch, "E107.3.24", {"start": v(-2.65, 3.96) * mm, "end": v(-2.7, 4.05) * mm});
            skLineSegment(sketch, "E107.3.25", {"start": v(-6.2, 3.13) * mm, "end": v(-6.32, 3.1) * mm});
            skLineSegment(sketch, "E107.3.26", {"start": v(-3.2, 4.9) * mm, "end": v(-3.21, 4.99) * mm});
            skLineSegment(sketch, "E107.3.27", {"start": v(-4.63, 3.14) * mm, "end": v(-4.71, 3.16) * mm});
            skLineSegment(sketch, "E107.3.28", {"start": v(-4.05, 2.7) * mm, "end": v(-4.13, 2.76) * mm});
            skLineSegment(sketch, "E107.3.29", {"start": v(-2.9, 4.3) * mm, "end": v(-2.98, 4.38) * mm});
            skLineSegment(sketch, "E107.3.30", {"start": v(-3.22, 5.08) * mm, "end": v(-3.23, 5.18) * mm});
            skLineSegment(sketch, "E107.3.31", {"start": v(-3.22, 5.68) * mm, "end": v(-3.2, 5.78) * mm});
            skLineSegment(sketch, "E107.3.32", {"start": v(-2.57, 3.8) * mm, "end": v(-2.6, 3.88) * mm});
            skLineSegment(sketch, "E107.3.33", {"start": v(-2.52, 3.15) * mm, "end": v(-2.5, 3.22) * mm});
            skLineSegment(sketch, "E107.3.34", {"start": v(-2.5, 3.54) * mm, "end": v(-2.51, 3.63) * mm});
            skLineSegment(sketch, "E107.3.35", {"start": v(-5.47, 3.23) * mm, "end": v(-5.58, 3.23) * mm});
            skLineSegment(sketch, "E107.3.36", {"start": v(-4.8, 3.18) * mm, "end": v(-4.9, 3.2) * mm});
            skLineSegment(sketch, "E107.3.37", {"start": v(-2.5, 3.3) * mm, "end": v(-2.49, 3.38) * mm});
            skLineSegment(sketch, "E107.3.38", {"start": v(-5.68, 3.22) * mm, "end": v(-5.78, 3.2) * mm});
            skLineSegment(sketch, "E107.3.39", {"start": v(-4.99, 3.21) * mm, "end": v(-5.08, 3.22) * mm});
            skLineSegment(sketch, "E107.3.40", {"start": v(-3.21, 4.99) * mm, "end": v(-3.22, 5.08) * mm});
            skLineSegment(sketch, "E107.3.41", {"start": v(-2.8, 6.55) * mm, "end": v(-2.73, 6.58) * mm});
            skLineSegment(sketch, "E107.3.42", {"start": v(-3.46, 2.49) * mm, "end": v(-3.54, 2.5) * mm});
            skLineSegment(sketch, "E107.3.43", {"start": v(-3.54, 2.5) * mm, "end": v(-3.63, 2.51) * mm});
            skLineSegment(sketch, "E107.3.44", {"start": v(-3.63, 2.51) * mm, "end": v(-3.71, 2.54) * mm});
            skLineSegment(sketch, "E107.3.45", {"start": v(-2.9, 2.65) * mm, "end": v(-2.99, 2.6) * mm});
            skLineSegment(sketch, "E107.3.46", {"start": v(-2.99, 2.6) * mm, "end": v(-3.06, 2.56) * mm});
            skLineSegment(sketch, "E107.3.47", {"start": v(-3.06, 2.56) * mm, "end": v(-3.15, 2.52) * mm});
            skLineSegment(sketch, "E107.3.48", {"start": v(-3.15, 2.52) * mm, "end": v(-3.22, 2.5) * mm});
            skLineSegment(sketch, "E107.3.49", {"start": v(-3.22, 2.5) * mm, "end": v(-3.3, 2.5) * mm});
            skLineSegment(sketch, "E107.3.50", {"start": v(-3.3, 2.5) * mm, "end": v(-3.38, 2.49) * mm});
            skLineSegment(sketch, "E107.3.51", {"start": v(-3.38, 2.49) * mm, "end": v(-3.46, 2.49) * mm});
            skLineSegment(sketch, "E107.3.52", {"start": v(-3.23, 5.18) * mm, "end": v(-3.23, 5.27) * mm});
            skLineSegment(sketch, "E107.3.53", {"start": v(-5.78, 3.2) * mm, "end": v(-5.89, 3.2) * mm});
            skLineSegment(sketch, "E107.3.54", {"start": v(-3.2, 5.89) * mm, "end": v(-3.18, 6) * mm});
            skLineSegment(sketch, "E107.3.55", {"start": v(-2.49, 3.38) * mm, "end": v(-2.49, 3.46) * mm});
            skLineSegment(sketch, "E107.3.56", {"start": v(-3.71, 2.54) * mm, "end": v(-3.8, 2.57) * mm});
            skLineSegment(sketch, "E107.3.57", {"start": v(-3.23, 5.47) * mm, "end": v(-3.23, 5.58) * mm});
            skLineSegment(sketch, "E107.3.58", {"start": v(-5.08, 3.22) * mm, "end": v(-5.18, 3.23) * mm});
            skLineSegment(sketch, "E107.3.59", {"start": v(-5.89, 3.2) * mm, "end": v(-6, 3.18) * mm});
            skLineSegment(sketch, "E107.3.60", {"start": v(-4.38, 2.98) * mm, "end": v(-4.47, 3.07) * mm});
            skLineSegment(sketch, "E107.3.61", {"start": v(-2.98, 4.38) * mm, "end": v(-3.07, 4.47) * mm});
            skLineSegment(sketch, "E107.3.62", {"start": v(-3.14, 4.63) * mm, "end": v(-3.16, 4.71) * mm});
            skLineSegment(sketch, "E107.3.63", {"start": v(-3.8, 2.57) * mm, "end": v(-3.88, 2.6) * mm});
            skLineSegment(sketch, "E107.3.64", {"start": v(-2.54, 3.71) * mm, "end": v(-2.57, 3.8) * mm});
            skLineSegment(sketch, "E107.3.65", {"start": v(-5.18, 3.23) * mm, "end": v(-5.27, 3.23) * mm});
            skLineSegment(sketch, "E107.3.66", {"start": v(-3.18, 6) * mm, "end": v(-3.16, 6.1) * mm});
            skLineSegment(sketch, "E107.3.67", {"start": v(-6, 3.18) * mm, "end": v(-6.1, 3.16) * mm});
            skLineSegment(sketch, "E107.3.68", {"start": v(-4.47, 3.07) * mm, "end": v(-4.54, 3.1) * mm});
            skLineSegment(sketch, "E107.3.69", {"start": v(-2.76, 4.13) * mm, "end": v(-2.82, 4.22) * mm});
            skLineSegment(sketch, "E107.3.70", {"start": v(-3.13, 6.2) * mm, "end": v(-3.1, 6.32) * mm});
            skLineSegment(sketch, "E107.3.71", {"start": v(-3.88, 2.6) * mm, "end": v(-3.96, 2.65) * mm});
            skLineSegment(sketch, "E107.3.72", {"start": v(-3.16, 6.1) * mm, "end": v(-3.13, 6.2) * mm});
            skLineSegment(sketch, "E107.3.73", {"start": v(-3.23, 5.27) * mm, "end": v(-3.23, 5.37) * mm});
            skLineSegment(sketch, "E107.3.74", {"start": v(-5.27, 3.23) * mm, "end": v(-5.37, 3.23) * mm});
            skLineSegment(sketch, "E107.3.75", {"start": v(-3.07, 4.47) * mm, "end": v(-3.1, 4.54) * mm});
            skLineSegment(sketch, "E107.3.76", {"start": v(-4.13, 2.76) * mm, "end": v(-4.22, 2.82) * mm});
            skLineSegment(sketch, "E107.3.77", {"start": v(-4.22, 2.82) * mm, "end": v(-4.3, 2.9) * mm});
            skLineSegment(sketch, "E107.3.78", {"start": v(-4.3, 2.9) * mm, "end": v(-4.38, 2.98) * mm});
            skLineSegment(sketch, "E107.3.79", {"start": v(-6.55, 2.8) * mm, "end": v(-6.58, 2.73) * mm});
            skLineSegment(sketch, "E107.3.80", {"start": v(-3, 6.46) * mm, "end": v(-2.94, 6.5) * mm});
            skLineSegment(sketch, "E107.3.81", {"start": v(-2.87, 6.52) * mm, "end": v(-2.8, 6.55) * mm});
            skLineSegment(sketch, "E107.3.82", {"start": v(-2.94, 6.5) * mm, "end": v(-2.87, 6.52) * mm});
            skLineSegment(sketch, "E107.3.83", {"start": v(-6.46, 3) * mm, "end": v(-6.5, 2.94) * mm});
            skLineSegment(sketch, "E107.3.84", {"start": v(-3.08, 6.43) * mm, "end": v(-3, 6.46) * mm});
            skLineSegment(sketch, "E107.3.85", {"start": v(-6.43, 3.08) * mm, "end": v(-6.46, 3) * mm});
            skLineSegment(sketch, "E107.3.86", {"start": v(-6.5, 2.94) * mm, "end": v(-6.52, 2.87) * mm});
            skLineSegment(sketch, "E107.3.87", {"start": v(-2.65, 2.9) * mm, "end": v(-2.6, 2.99) * mm});
            skLineSegment(sketch, "E107.3.88", {"start": v(-6.52, 2.87) * mm, "end": v(-6.55, 2.8) * mm});
            skLineSegment(sketch, "E107.3.89", {"start": v(-2.6, 2.99) * mm, "end": v(-2.56, 3.06) * mm});
            skLineSegment(sketch, "E107.3.90", {"start": v(-2.73, 2.82) * mm, "end": v(-2.65, 2.9) * mm});
            skLineSegment(sketch, "E107.3.91", {"start": v(-2.75, 2.79) * mm, "end": v(-2.74, 2.8) * mm});
            skLineSegment(sketch, "E107.3.92", {"start": v(-2.78, 2.76) * mm, "end": v(-2.79, 2.75) * mm});
            skLineSegment(sketch, "E107.3.93", {"start": v(-2.82, 2.73) * mm, "end": v(-2.9, 2.65) * mm});
            skLineSegment(sketch, "E107.3.94", {"start": v(-2.8, 2.74) * mm, "end": v(-2.82, 2.73) * mm});
            skLineSegment(sketch, "E107.3.95", {"start": v(-2.8, 2.74) * mm, "end": v(-2.8, 2.74) * mm});
            skLineSegment(sketch, "E107.3.96", {"start": v(-2.79, 2.75) * mm, "end": v(-2.8, 2.74) * mm});
            skLineSegment(sketch, "E107.3.97", {"start": v(-2.77, 2.77) * mm, "end": v(-2.78, 2.76) * mm});
            skLineSegment(sketch, "E107.3.98", {"start": v(-2.77, 2.77) * mm, "end": v(-2.76, 2.78) * mm});
            skLineSegment(sketch, "E107.3.99", {"start": v(-2.76, 2.78) * mm, "end": v(-2.75, 2.79) * mm});
            skLineSegment(sketch, "E107.3.100", {"start": v(-2.74, 2.8) * mm, "end": v(-2.74, 2.8) * mm});
            skLineSegment(sketch, "E107.3.101", {"start": v(-2.74, 2.8) * mm, "end": v(-2.73, 2.82) * mm});
            skPoint(sketch, "E107.4.0", {"position": v(-5.7, 0) * mm});
            skPoint(sketch, "E107.4.1", {"position": v(-5.7, 0) * mm});
            skLineSegment(sketch, "E107.4.2", {"start": v(-4.98, 0.99) * mm, "end": v(-5.1, 1) * mm});
            skLineSegment(sketch, "E107.4.3", {"start": v(-6.23, 1.66) * mm, "end": v(-6.3, 1.74) * mm});
            skLineSegment(sketch, "E107.4.4", {"start": v(-6.09, 1.51) * mm, "end": v(-6.16, 1.58) * mm});
            skLineSegment(sketch, "E107.4.5", {"start": v(-6.55, -2.08) * mm, "end": v(-6.6, -2.17) * mm});
            skLineSegment(sketch, "E107.4.6", {"start": v(-5.41, -1.02) * mm, "end": v(-5.49, -1.06) * mm});
            skLineSegment(sketch, "E107.4.7", {"start": v(-6.36, 1.82) * mm, "end": v(-6.42, 1.9) * mm});
            skLineSegment(sketch, "E107.4.8", {"start": v(-4.67, -0.93) * mm, "end": v(-4.77, -0.96) * mm});
            skLineSegment(sketch, "E107.4.9", {"start": v(-3.97, 0.36) * mm, "end": v(-4, 0.44) * mm});
            skLineSegment(sketch, "E107.4.10", {"start": v(-5.65, 1.15) * mm, "end": v(-5.72, 1.2) * mm});
            skLineSegment(sketch, "E107.4.11", {"start": v(-6.09, -1.51) * mm, "end": v(-6.16, -1.58) * mm});
            skLineSegment(sketch, "E107.4.12", {"start": v(-6.66, -2.27) * mm, "end": v(-6.72, -2.37) * mm});
            skLineSegment(sketch, "E107.4.13", {"start": v(-4.2, 0.69) * mm, "end": v(-4.27, 0.74) * mm});
            skLineSegment(sketch, "E107.4.14", {"start": v(-5.57, -1.1) * mm, "end": v(-5.65, -1.15) * mm});
            skLineSegment(sketch, "E107.4.15", {"start": v(-4.77, 0.96) * mm, "end": v(-4.87, 0.97) * mm});
            skLineSegment(sketch, "E107.4.16", {"start": v(-4.58, 0.9) * mm, "end": v(-4.67, 0.93) * mm});
            skLineSegment(sketch, "E107.4.17", {"start": v(-5.41, 1.02) * mm, "end": v(-5.49, 1.06) * mm});
            skLineSegment(sketch, "E107.4.18", {"start": v(-4.34, 0.79) * mm, "end": v(-4.42, 0.83) * mm});
            skLineSegment(sketch, "E107.4.19", {"start": v(-6.66, 2.27) * mm, "end": v(-6.72, 2.37) * mm});
            skLineSegment(sketch, "E107.4.20", {"start": v(-4.05, 0.5) * mm, "end": v(-4.1, 0.57) * mm});
            skLineSegment(sketch, "E107.4.21", {"start": v(-6.23, -1.66) * mm, "end": v(-6.3, -1.74) * mm});
            skLineSegment(sketch, "E107.4.22", {"start": v(-5.72, -1.2) * mm, "end": v(-5.8, -1.25) * mm});
            skLineSegment(sketch, "E107.4.23", {"start": v(-5.57, 1.1) * mm, "end": v(-5.65, 1.15) * mm});
            skLineSegment(sketch, "E107.4.24", {"start": v(-4.67, 0.93) * mm, "end": v(-4.77, 0.96) * mm});
            skLineSegment(sketch, "E107.4.25", {"start": v(-6.6, -2.17) * mm, "end": v(-6.66, -2.27) * mm});
            skLineSegment(sketch, "E107.4.26", {"start": v(-5.72, 1.2) * mm, "end": v(-5.8, 1.25) * mm});
            skLineSegment(sketch, "E107.4.27", {"start": v(-5.49, -1.06) * mm, "end": v(-5.57, -1.1) * mm});
            skLineSegment(sketch, "E107.4.28", {"start": v(-4.77, -0.96) * mm, "end": v(-4.87, -0.97) * mm});
            skLineSegment(sketch, "E107.4.29", {"start": v(-5.1, 1) * mm, "end": v(-5.2, 0.99) * mm});
            skLineSegment(sketch, "E107.4.30", {"start": v(-5.87, 1.31) * mm, "end": v(-5.94, 1.38) * mm});
            skLineSegment(sketch, "E107.4.31", {"start": v(-6.3, 1.74) * mm, "end": v(-6.36, 1.82) * mm});
            skLineSegment(sketch, "E107.4.32", {"start": v(-4.5, 0.87) * mm, "end": v(-4.58, 0.9) * mm});
            skLineSegment(sketch, "E107.4.33", {"start": v(-4, 0.44) * mm, "end": v(-4.05, 0.5) * mm});
            skLineSegment(sketch, "E107.4.34", {"start": v(-4.27, 0.74) * mm, "end": v(-4.34, 0.79) * mm});
            skLineSegment(sketch, "E107.4.35", {"start": v(-6.16, -1.58) * mm, "end": v(-6.23, -1.66) * mm});
            skLineSegment(sketch, "E107.4.36", {"start": v(-5.65, -1.15) * mm, "end": v(-5.72, -1.2) * mm});
            skLineSegment(sketch, "E107.4.37", {"start": v(-4.1, 0.57) * mm, "end": v(-4.15, 0.63) * mm});
            skLineSegment(sketch, "E107.4.38", {"start": v(-6.3, -1.74) * mm, "end": v(-6.36, -1.82) * mm});
            skLineSegment(sketch, "E107.4.39", {"start": v(-5.8, -1.25) * mm, "end": v(-5.87, -1.31) * mm});
            skLineSegment(sketch, "E107.4.40", {"start": v(-5.8, 1.25) * mm, "end": v(-5.87, 1.31) * mm});
            skLineSegment(sketch, "E107.4.41", {"start": v(-6.61, 2.66) * mm, "end": v(-6.58, 2.73) * mm});
            skLineSegment(sketch, "E107.4.42", {"start": v(-4.2, -0.69) * mm, "end": v(-4.27, -0.74) * mm});
            skLineSegment(sketch, "E107.4.43", {"start": v(-4.27, -0.74) * mm, "end": v(-4.34, -0.79) * mm});
            skLineSegment(sketch, "E107.4.44", {"start": v(-4.34, -0.79) * mm, "end": v(-4.42, -0.83) * mm});
            skLineSegment(sketch, "E107.4.45", {"start": v(-3.93, -0.18) * mm, "end": v(-3.95, -0.28) * mm});
            skLineSegment(sketch, "E107.4.46", {"start": v(-3.95, -0.28) * mm, "end": v(-3.97, -0.36) * mm});
            skLineSegment(sketch, "E107.4.47", {"start": v(-3.97, -0.36) * mm, "end": v(-4, -0.44) * mm});
            skLineSegment(sketch, "E107.4.48", {"start": v(-4, -0.44) * mm, "end": v(-4.05, -0.5) * mm});
            skLineSegment(sketch, "E107.4.49", {"start": v(-4.05, -0.5) * mm, "end": v(-4.1, -0.57) * mm});
            skLineSegment(sketch, "E107.4.50", {"start": v(-4.1, -0.57) * mm, "end": v(-4.15, -0.63) * mm});
            skLineSegment(sketch, "E107.4.51", {"start": v(-4.15, -0.63) * mm, "end": v(-4.2, -0.69) * mm});
            skLineSegment(sketch, "E107.4.52", {"start": v(-5.94, 1.38) * mm, "end": v(-6.02, 1.44) * mm});
            skLineSegment(sketch, "E107.4.53", {"start": v(-6.36, -1.82) * mm, "end": v(-6.42, -1.9) * mm});
            skLineSegment(sketch, "E107.4.54", {"start": v(-6.42, 1.9) * mm, "end": v(-6.48, 2) * mm});
            skLineSegment(sketch, "E107.4.55", {"start": v(-4.15, 0.63) * mm, "end": v(-4.2, 0.69) * mm});
            skLineSegment(sketch, "E107.4.56", {"start": v(-4.42, -0.83) * mm, "end": v(-4.5, -0.87) * mm});
            skLineSegment(sketch, "E107.4.57", {"start": v(-6.16, 1.58) * mm, "end": v(-6.23, 1.66) * mm});
            skLineSegment(sketch, "E107.4.58", {"start": v(-5.87, -1.31) * mm, "end": v(-5.94, -1.38) * mm});
            skLineSegment(sketch, "E107.4.59", {"start": v(-6.42, -1.9) * mm, "end": v(-6.48, -2) * mm});
            skLineSegment(sketch, "E107.4.60", {"start": v(-5.2, -0.99) * mm, "end": v(-5.33, -0.99) * mm});
            skLineSegment(sketch, "E107.4.61", {"start": v(-5.2, 0.99) * mm, "end": v(-5.33, 0.99) * mm});
            skLineSegment(sketch, "E107.4.62", {"start": v(-5.49, 1.06) * mm, "end": v(-5.57, 1.1) * mm});
            skLineSegment(sketch, "E107.4.63", {"start": v(-4.5, -0.87) * mm, "end": v(-4.58, -0.9) * mm});
            skLineSegment(sketch, "E107.4.64", {"start": v(-4.42, 0.83) * mm, "end": v(-4.5, 0.87) * mm});
            skLineSegment(sketch, "E107.4.65", {"start": v(-5.94, -1.38) * mm, "end": v(-6.02, -1.44) * mm});
            skLineSegment(sketch, "E107.4.66", {"start": v(-6.48, 2) * mm, "end": v(-6.55, 2.08) * mm});
            skLineSegment(sketch, "E107.4.67", {"start": v(-6.48, -2) * mm, "end": v(-6.55, -2.08) * mm});
            skLineSegment(sketch, "E107.4.68", {"start": v(-5.33, -0.99) * mm, "end": v(-5.41, -1.02) * mm});
            skLineSegment(sketch, "E107.4.69", {"start": v(-4.87, 0.97) * mm, "end": v(-4.98, 0.99) * mm});
            skLineSegment(sketch, "E107.4.70", {"start": v(-6.6, 2.17) * mm, "end": v(-6.66, 2.27) * mm});
            skLineSegment(sketch, "E107.4.71", {"start": v(-4.58, -0.9) * mm, "end": v(-4.67, -0.93) * mm});
            skLineSegment(sketch, "E107.4.72", {"start": v(-6.55, 2.08) * mm, "end": v(-6.6, 2.17) * mm});
            skLineSegment(sketch, "E107.4.73", {"start": v(-6.02, 1.44) * mm, "end": v(-6.09, 1.51) * mm});
            skLineSegment(sketch, "E107.4.74", {"start": v(-6.02, -1.44) * mm, "end": v(-6.09, -1.51) * mm});
            skLineSegment(sketch, "E107.4.75", {"start": v(-5.33, 0.99) * mm, "end": v(-5.41, 1.02) * mm});
            skLineSegment(sketch, "E107.4.76", {"start": v(-4.87, -0.97) * mm, "end": v(-4.98, -0.99) * mm});
            skLineSegment(sketch, "E107.4.77", {"start": v(-4.98, -0.99) * mm, "end": v(-5.1, -1) * mm});
            skLineSegment(sketch, "E107.4.78", {"start": v(-5.1, -1) * mm, "end": v(-5.2, -0.99) * mm});
            skLineSegment(sketch, "E107.4.79", {"start": v(-6.61, -2.66) * mm, "end": v(-6.58, -2.73) * mm});
            skLineSegment(sketch, "E107.4.80", {"start": v(-6.7, 2.44) * mm, "end": v(-6.67, 2.51) * mm});
            skLineSegment(sketch, "E107.4.81", {"start": v(-6.64, 2.58) * mm, "end": v(-6.61, 2.66) * mm});
            skLineSegment(sketch, "E107.4.82", {"start": v(-6.67, 2.51) * mm, "end": v(-6.64, 2.58) * mm});
            skLineSegment(sketch, "E107.4.83", {"start": v(-6.7, -2.44) * mm, "end": v(-6.67, -2.51) * mm});
            skLineSegment(sketch, "E107.4.84", {"start": v(-6.72, 2.37) * mm, "end": v(-6.7, 2.44) * mm});
            skLineSegment(sketch, "E107.4.85", {"start": v(-6.72, -2.37) * mm, "end": v(-6.7, -2.44) * mm});
            skLineSegment(sketch, "E107.4.86", {"start": v(-6.67, -2.51) * mm, "end": v(-6.64, -2.58) * mm});
            skLineSegment(sketch, "E107.4.87", {"start": v(-3.93, 0.18) * mm, "end": v(-3.95, 0.28) * mm});
            skLineSegment(sketch, "E107.4.88", {"start": v(-6.64, -2.58) * mm, "end": v(-6.61, -2.66) * mm});
            skLineSegment(sketch, "E107.4.89", {"start": v(-3.95, 0.28) * mm, "end": v(-3.97, 0.36) * mm});
            skLineSegment(sketch, "E107.4.90", {"start": v(-3.92, 0.06) * mm, "end": v(-3.93, 0.18) * mm});
            skLineSegment(sketch, "E107.4.91", {"start": v(-3.92, 0.03) * mm, "end": v(-3.92, 0.04) * mm});
            skLineSegment(sketch, "E107.4.92", {"start": v(-3.92, -0.01) * mm, "end": v(-3.92, -0.03) * mm});
            skLineSegment(sketch, "E107.4.93", {"start": v(-3.92, -0.06) * mm, "end": v(-3.93, -0.18) * mm});
            skLineSegment(sketch, "E107.4.94", {"start": v(-3.92, -0.05) * mm, "end": v(-3.92, -0.06) * mm});
            skLineSegment(sketch, "E107.4.95", {"start": v(-3.92, -0.04) * mm, "end": v(-3.92, -0.05) * mm});
            skLineSegment(sketch, "E107.4.96", {"start": v(-3.92, -0.03) * mm, "end": v(-3.92, -0.04) * mm});
            skLineSegment(sketch, "E107.4.97", {"start": v(-3.92, 0) * mm, "end": v(-3.92, -0.01) * mm});
            skLineSegment(sketch, "E107.4.98", {"start": v(-3.92, 0) * mm, "end": v(-3.92, 0.01) * mm});
            skLineSegment(sketch, "E107.4.99", {"start": v(-3.92, 0.01) * mm, "end": v(-3.92, 0.03) * mm});
            skLineSegment(sketch, "E107.4.100", {"start": v(-3.92, 0.04) * mm, "end": v(-3.92, 0.05) * mm});
            skLineSegment(sketch, "E107.4.101", {"start": v(-3.92, 0.05) * mm, "end": v(-3.92, 0.06) * mm});
            skPoint(sketch, "E107.5.0", {"position": v(-4.03, -4.03) * mm});
            skPoint(sketch, "E107.5.1", {"position": v(-4.03, -4.03) * mm});
            skLineSegment(sketch, "E107.5.2", {"start": v(-4.22, -2.82) * mm, "end": v(-4.3, -2.9) * mm});
            skLineSegment(sketch, "E107.5.3", {"start": v(-5.58, -3.23) * mm, "end": v(-5.68, -3.22) * mm});
            skLineSegment(sketch, "E107.5.4", {"start": v(-5.37, -3.23) * mm, "end": v(-5.47, -3.23) * mm});
            skLineSegment(sketch, "E107.5.5", {"start": v(-3.16, -6.1) * mm, "end": v(-3.13, -6.2) * mm});
            skLineSegment(sketch, "E107.5.6", {"start": v(-3.1, -4.54) * mm, "end": v(-3.14, -4.63) * mm});
            skLineSegment(sketch, "E107.5.7", {"start": v(-5.78, -3.2) * mm, "end": v(-5.89, -3.2) * mm});
            skLineSegment(sketch, "E107.5.8", {"start": v(-2.65, -3.96) * mm, "end": v(-2.7, -4.05) * mm});
            skLineSegment(sketch, "E107.5.9", {"start": v(-3.06, -2.56) * mm, "end": v(-3.15, -2.52) * mm});
            skLineSegment(sketch, "E107.5.10", {"start": v(-4.8, -3.18) * mm, "end": v(-4.9, -3.2) * mm});
            skLineSegment(sketch, "E107.5.11", {"start": v(-3.23, -5.37) * mm, "end": v(-3.23, -5.47) * mm});
            skLineSegment(sketch, "E107.5.12", {"start": v(-3.1, -6.32) * mm, "end": v(-3.08, -6.43) * mm});
            skLineSegment(sketch, "E107.5.13", {"start": v(-3.46, -2.49) * mm, "end": v(-3.54, -2.5) * mm});
            skLineSegment(sketch, "E107.5.14", {"start": v(-3.16, -4.71) * mm, "end": v(-3.18, -4.8) * mm});
            skLineSegment(sketch, "E107.5.15", {"start": v(-4.05, -2.7) * mm, "end": v(-4.13, -2.76) * mm});
            skLineSegment(sketch, "E107.5.16", {"start": v(-3.88, -2.6) * mm, "end": v(-3.96, -2.65) * mm});
            skLineSegment(sketch, "E107.5.17", {"start": v(-4.54, -3.1) * mm, "end": v(-4.63, -3.14) * mm});
            skLineSegment(sketch, "E107.5.18", {"start": v(-3.63, -2.51) * mm, "end": v(-3.71, -2.54) * mm});
            skLineSegment(sketch, "E107.5.19", {"start": v(-6.32, -3.1) * mm, "end": v(-6.43, -3.08) * mm});
            skLineSegment(sketch, "E107.5.20", {"start": v(-3.22, -2.5) * mm, "end": v(-3.3, -2.5) * mm});
            skLineSegment(sketch, "E107.5.21", {"start": v(-3.23, -5.58) * mm, "end": v(-3.22, -5.68) * mm});
            skLineSegment(sketch, "E107.5.22", {"start": v(-3.2, -4.9) * mm, "end": v(-3.21, -4.99) * mm});
            skLineSegment(sketch, "E107.5.23", {"start": v(-4.71, -3.16) * mm, "end": v(-4.8, -3.18) * mm});
            skLineSegment(sketch, "E107.5.24", {"start": v(-3.96, -2.65) * mm, "end": v(-4.05, -2.7) * mm});
            skLineSegment(sketch, "E107.5.25", {"start": v(-3.13, -6.2) * mm, "end": v(-3.1, -6.32) * mm});
            skLineSegment(sketch, "E107.5.26", {"start": v(-4.9, -3.2) * mm, "end": v(-4.99, -3.21) * mm});
            skLineSegment(sketch, "E107.5.27", {"start": v(-3.14, -4.63) * mm, "end": v(-3.16, -4.71) * mm});
            skLineSegment(sketch, "E107.5.28", {"start": v(-2.7, -4.05) * mm, "end": v(-2.76, -4.13) * mm});
            skLineSegment(sketch, "E107.5.29", {"start": v(-4.3, -2.9) * mm, "end": v(-4.38, -2.98) * mm});
            skLineSegment(sketch, "E107.5.30", {"start": v(-5.08, -3.22) * mm, "end": v(-5.18, -3.23) * mm});
            skLineSegment(sketch, "E107.5.31", {"start": v(-5.68, -3.22) * mm, "end": v(-5.78, -3.2) * mm});
            skLineSegment(sketch, "E107.5.32", {"start": v(-3.8, -2.57) * mm, "end": v(-3.88, -2.6) * mm});
            skLineSegment(sketch, "E107.5.33", {"start": v(-3.15, -2.52) * mm, "end": v(-3.22, -2.5) * mm});
            skLineSegment(sketch, "E107.5.34", {"start": v(-3.54, -2.5) * mm, "end": v(-3.63, -2.51) * mm});
            skLineSegment(sketch, "E107.5.35", {"start": v(-3.23, -5.47) * mm, "end": v(-3.23, -5.58) * mm});
            skLineSegment(sketch, "E107.5.36", {"start": v(-3.18, -4.8) * mm, "end": v(-3.2, -4.9) * mm});
            skLineSegment(sketch, "E107.5.37", {"start": v(-3.3, -2.5) * mm, "end": v(-3.38, -2.49) * mm});
            skLineSegment(sketch, "E107.5.38", {"start": v(-3.22, -5.68) * mm, "end": v(-3.2, -5.78) * mm});
            skLineSegment(sketch, "E107.5.39", {"start": v(-3.21, -4.99) * mm, "end": v(-3.22, -5.08) * mm});
            skLineSegment(sketch, "E107.5.40", {"start": v(-4.99, -3.21) * mm, "end": v(-5.08, -3.22) * mm});
            skLineSegment(sketch, "E107.5.41", {"start": v(-6.55, -2.8) * mm, "end": v(-6.58, -2.73) * mm});
            skLineSegment(sketch, "E107.5.42", {"start": v(-2.49, -3.46) * mm, "end": v(-2.5, -3.54) * mm});
            skLineSegment(sketch, "E107.5.43", {"start": v(-2.5, -3.54) * mm, "end": v(-2.51, -3.63) * mm});
            skLineSegment(sketch, "E107.5.44", {"start": v(-2.51, -3.63) * mm, "end": v(-2.54, -3.71) * mm});
            skLineSegment(sketch, "E107.5.45", {"start": v(-2.65, -2.9) * mm, "end": v(-2.6, -2.99) * mm});
            skLineSegment(sketch, "E107.5.46", {"start": v(-2.6, -2.99) * mm, "end": v(-2.56, -3.06) * mm});
            skLineSegment(sketch, "E107.5.47", {"start": v(-2.56, -3.06) * mm, "end": v(-2.52, -3.15) * mm});
            skLineSegment(sketch, "E107.5.48", {"start": v(-2.52, -3.15) * mm, "end": v(-2.5, -3.22) * mm});
            skLineSegment(sketch, "E107.5.49", {"start": v(-2.5, -3.22) * mm, "end": v(-2.5, -3.3) * mm});
            skLineSegment(sketch, "E107.5.50", {"start": v(-2.5, -3.3) * mm, "end": v(-2.49, -3.38) * mm});
            skLineSegment(sketch, "E107.5.51", {"start": v(-2.49, -3.38) * mm, "end": v(-2.49, -3.46) * mm});
            skLineSegment(sketch, "E107.5.52", {"start": v(-5.18, -3.23) * mm, "end": v(-5.27, -3.23) * mm});
            skLineSegment(sketch, "E107.5.53", {"start": v(-3.2, -5.78) * mm, "end": v(-3.2, -5.89) * mm});
            skLineSegment(sketch, "E107.5.54", {"start": v(-5.89, -3.2) * mm, "end": v(-6, -3.18) * mm});
            skLineSegment(sketch, "E107.5.55", {"start": v(-3.38, -2.49) * mm, "end": v(-3.46, -2.49) * mm});
            skLineSegment(sketch, "E107.5.56", {"start": v(-2.54, -3.71) * mm, "end": v(-2.57, -3.8) * mm});
            skLineSegment(sketch, "E107.5.57", {"start": v(-5.47, -3.23) * mm, "end": v(-5.58, -3.23) * mm});
            skLineSegment(sketch, "E107.5.58", {"start": v(-3.22, -5.08) * mm, "end": v(-3.23, -5.18) * mm});
            skLineSegment(sketch, "E107.5.59", {"start": v(-3.2, -5.89) * mm, "end": v(-3.18, -6) * mm});
            skLineSegment(sketch, "E107.5.60", {"start": v(-2.98, -4.38) * mm, "end": v(-3.07, -4.47) * mm});
            skLineSegment(sketch, "E107.5.61", {"start": v(-4.38, -2.98) * mm, "end": v(-4.47, -3.07) * mm});
            skLineSegment(sketch, "E107.5.62", {"start": v(-4.63, -3.14) * mm, "end": v(-4.71, -3.16) * mm});
            skLineSegment(sketch, "E107.5.63", {"start": v(-2.57, -3.8) * mm, "end": v(-2.6, -3.88) * mm});
            skLineSegment(sketch, "E107.5.64", {"start": v(-3.71, -2.54) * mm, "end": v(-3.8, -2.57) * mm});
            skLineSegment(sketch, "E107.5.65", {"start": v(-3.23, -5.18) * mm, "end": v(-3.23, -5.27) * mm});
            skLineSegment(sketch, "E107.5.66", {"start": v(-6, -3.18) * mm, "end": v(-6.1, -3.16) * mm});
            skLineSegment(sketch, "E107.5.67", {"start": v(-3.18, -6) * mm, "end": v(-3.16, -6.1) * mm});
            skLineSegment(sketch, "E107.5.68", {"start": v(-3.07, -4.47) * mm, "end": v(-3.1, -4.54) * mm});
            skLineSegment(sketch, "E107.5.69", {"start": v(-4.13, -2.76) * mm, "end": v(-4.22, -2.82) * mm});
            skLineSegment(sketch, "E107.5.70", {"start": v(-6.2, -3.13) * mm, "end": v(-6.32, -3.1) * mm});
            skLineSegment(sketch, "E107.5.71", {"start": v(-2.6, -3.88) * mm, "end": v(-2.65, -3.96) * mm});
            skLineSegment(sketch, "E107.5.72", {"start": v(-6.1, -3.16) * mm, "end": v(-6.2, -3.13) * mm});
            skLineSegment(sketch, "E107.5.73", {"start": v(-5.27, -3.23) * mm, "end": v(-5.37, -3.23) * mm});
            skLineSegment(sketch, "E107.5.74", {"start": v(-3.23, -5.27) * mm, "end": v(-3.23, -5.37) * mm});
            skLineSegment(sketch, "E107.5.75", {"start": v(-4.47, -3.07) * mm, "end": v(-4.54, -3.1) * mm});
            skLineSegment(sketch, "E107.5.76", {"start": v(-2.76, -4.13) * mm, "end": v(-2.82, -4.22) * mm});
            skLineSegment(sketch, "E107.5.77", {"start": v(-2.82, -4.22) * mm, "end": v(-2.9, -4.3) * mm});
            skLineSegment(sketch, "E107.5.78", {"start": v(-2.9, -4.3) * mm, "end": v(-2.98, -4.38) * mm});
            skLineSegment(sketch, "E107.5.79", {"start": v(-2.8, -6.55) * mm, "end": v(-2.73, -6.58) * mm});
            skLineSegment(sketch, "E107.5.80", {"start": v(-6.46, -3) * mm, "end": v(-6.5, -2.94) * mm});
            skLineSegment(sketch, "E107.5.81", {"start": v(-6.52, -2.87) * mm, "end": v(-6.55, -2.8) * mm});
            skLineSegment(sketch, "E107.5.82", {"start": v(-6.5, -2.94) * mm, "end": v(-6.52, -2.87) * mm});
            skLineSegment(sketch, "E107.5.83", {"start": v(-3, -6.46) * mm, "end": v(-2.94, -6.5) * mm});
            skLineSegment(sketch, "E107.5.84", {"start": v(-6.43, -3.08) * mm, "end": v(-6.46, -3) * mm});
            skLineSegment(sketch, "E107.5.85", {"start": v(-3.08, -6.43) * mm, "end": v(-3, -6.46) * mm});
            skLineSegment(sketch, "E107.5.86", {"start": v(-2.94, -6.5) * mm, "end": v(-2.87, -6.52) * mm});
            skLineSegment(sketch, "E107.5.87", {"start": v(-2.9, -2.65) * mm, "end": v(-2.99, -2.6) * mm});
            skLineSegment(sketch, "E107.5.88", {"start": v(-2.87, -6.52) * mm, "end": v(-2.8, -6.55) * mm});
            skLineSegment(sketch, "E107.5.89", {"start": v(-2.99, -2.6) * mm, "end": v(-3.06, -2.56) * mm});
            skLineSegment(sketch, "E107.5.90", {"start": v(-2.82, -2.73) * mm, "end": v(-2.9, -2.65) * mm});
            skLineSegment(sketch, "E107.5.91", {"start": v(-2.79, -2.75) * mm, "end": v(-2.8, -2.74) * mm});
            skLineSegment(sketch, "E107.5.92", {"start": v(-2.76, -2.78) * mm, "end": v(-2.75, -2.79) * mm});
            skLineSegment(sketch, "E107.5.93", {"start": v(-2.73, -2.82) * mm, "end": v(-2.65, -2.9) * mm});
            skLineSegment(sketch, "E107.5.94", {"start": v(-2.74, -2.8) * mm, "end": v(-2.73, -2.82) * mm});
            skLineSegment(sketch, "E107.5.95", {"start": v(-2.74, -2.8) * mm, "end": v(-2.74, -2.8) * mm});
            skLineSegment(sketch, "E107.5.96", {"start": v(-2.75, -2.79) * mm, "end": v(-2.74, -2.8) * mm});
            skLineSegment(sketch, "E107.5.97", {"start": v(-2.77, -2.77) * mm, "end": v(-2.76, -2.78) * mm});
            skLineSegment(sketch, "E107.5.98", {"start": v(-2.77, -2.77) * mm, "end": v(-2.78, -2.76) * mm});
            skLineSegment(sketch, "E107.5.99", {"start": v(-2.78, -2.76) * mm, "end": v(-2.79, -2.75) * mm});
            skLineSegment(sketch, "E107.5.100", {"start": v(-2.8, -2.74) * mm, "end": v(-2.8, -2.74) * mm});
            skLineSegment(sketch, "E107.5.101", {"start": v(-2.8, -2.74) * mm, "end": v(-2.82, -2.73) * mm});
            skLineSegment(sketch, "E107.6.2", {"start": v(-0.99, -4.98) * mm, "end": v(-1, -5.1) * mm});
            skLineSegment(sketch, "E107.6.3", {"start": v(-1.66, -6.23) * mm, "end": v(-1.74, -6.3) * mm});
            skLineSegment(sketch, "E107.6.4", {"start": v(-1.51, -6.09) * mm, "end": v(-1.58, -6.16) * mm});
            skLineSegment(sketch, "E107.6.5", {"start": v(2.08, -6.55) * mm, "end": v(2.17, -6.6) * mm});
            skLineSegment(sketch, "E107.6.6", {"start": v(1.02, -5.41) * mm, "end": v(1.06, -5.49) * mm});
            skLineSegment(sketch, "E107.6.7", {"start": v(-1.82, -6.36) * mm, "end": v(-1.9, -6.42) * mm});
            skLineSegment(sketch, "E107.6.8", {"start": v(0.93, -4.67) * mm, "end": v(0.96, -4.77) * mm});
            skLineSegment(sketch, "E107.6.9", {"start": v(-0.36, -3.97) * mm, "end": v(-0.44, -4) * mm});
            skLineSegment(sketch, "E107.6.10", {"start": v(-1.15, -5.65) * mm, "end": v(-1.2, -5.72) * mm});
            skLineSegment(sketch, "E107.6.11", {"start": v(1.51, -6.09) * mm, "end": v(1.58, -6.16) * mm});
            skLineSegment(sketch, "E107.6.12", {"start": v(2.27, -6.66) * mm, "end": v(2.37, -6.72) * mm});
            skLineSegment(sketch, "E107.6.13", {"start": v(-0.69, -4.2) * mm, "end": v(-0.74, -4.27) * mm});
            skLineSegment(sketch, "E107.6.14", {"start": v(1.1, -5.57) * mm, "end": v(1.15, -5.65) * mm});
            skLineSegment(sketch, "E107.6.15", {"start": v(-0.96, -4.77) * mm, "end": v(-0.97, -4.87) * mm});
            skLineSegment(sketch, "E107.6.16", {"start": v(-0.9, -4.58) * mm, "end": v(-0.93, -4.67) * mm});
            skLineSegment(sketch, "E107.6.17", {"start": v(-1.02, -5.41) * mm, "end": v(-1.06, -5.49) * mm});
            skLineSegment(sketch, "E107.6.18", {"start": v(-0.79, -4.34) * mm, "end": v(-0.83, -4.42) * mm});
            skLineSegment(sketch, "E107.6.19", {"start": v(-2.27, -6.66) * mm, "end": v(-2.37, -6.72) * mm});
            skLineSegment(sketch, "E107.6.20", {"start": v(-0.5, -4.05) * mm, "end": v(-0.57, -4.1) * mm});
            skLineSegment(sketch, "E107.6.21", {"start": v(1.66, -6.23) * mm, "end": v(1.74, -6.3) * mm});
            skLineSegment(sketch, "E107.6.22", {"start": v(1.2, -5.72) * mm, "end": v(1.25, -5.8) * mm});
            skLineSegment(sketch, "E107.6.23", {"start": v(-1.1, -5.57) * mm, "end": v(-1.15, -5.65) * mm});
            skLineSegment(sketch, "E107.6.24", {"start": v(-0.93, -4.67) * mm, "end": v(-0.96, -4.77) * mm});
            skLineSegment(sketch, "E107.6.25", {"start": v(2.17, -6.6) * mm, "end": v(2.27, -6.66) * mm});
            skLineSegment(sketch, "E107.6.26", {"start": v(-1.2, -5.72) * mm, "end": v(-1.25, -5.8) * mm});
            skLineSegment(sketch, "E107.6.27", {"start": v(1.06, -5.49) * mm, "end": v(1.1, -5.57) * mm});
            skLineSegment(sketch, "E107.6.28", {"start": v(0.96, -4.77) * mm, "end": v(0.97, -4.87) * mm});
            skLineSegment(sketch, "E107.6.29", {"start": v(-1, -5.1) * mm, "end": v(-0.99, -5.2) * mm});
            skLineSegment(sketch, "E107.6.30", {"start": v(-1.31, -5.87) * mm, "end": v(-1.38, -5.94) * mm});
            skLineSegment(sketch, "E107.6.31", {"start": v(-1.74, -6.3) * mm, "end": v(-1.82, -6.36) * mm});
            skLineSegment(sketch, "E107.6.32", {"start": v(-0.87, -4.5) * mm, "end": v(-0.9, -4.58) * mm});
            skLineSegment(sketch, "E107.6.33", {"start": v(-0.44, -4) * mm, "end": v(-0.5, -4.05) * mm});
            skLineSegment(sketch, "E107.6.34", {"start": v(-0.74, -4.27) * mm, "end": v(-0.79, -4.34) * mm});
            skLineSegment(sketch, "E107.6.35", {"start": v(1.58, -6.16) * mm, "end": v(1.66, -6.23) * mm});
            skLineSegment(sketch, "E107.6.36", {"start": v(1.15, -5.65) * mm, "end": v(1.2, -5.72) * mm});
            skLineSegment(sketch, "E107.6.37", {"start": v(-0.57, -4.1) * mm, "end": v(-0.63, -4.15) * mm});
            skLineSegment(sketch, "E107.6.38", {"start": v(1.74, -6.3) * mm, "end": v(1.82, -6.36) * mm});
            skLineSegment(sketch, "E107.6.39", {"start": v(1.25, -5.8) * mm, "end": v(1.31, -5.87) * mm});
            skLineSegment(sketch, "E107.6.40", {"start": v(-1.25, -5.8) * mm, "end": v(-1.31, -5.87) * mm});
            skLineSegment(sketch, "E107.6.41", {"start": v(-2.66, -6.61) * mm, "end": v(-2.73, -6.58) * mm});
            skLineSegment(sketch, "E107.6.42", {"start": v(0.69, -4.2) * mm, "end": v(0.74, -4.27) * mm});
            skLineSegment(sketch, "E107.6.43", {"start": v(0.74, -4.27) * mm, "end": v(0.79, -4.34) * mm});
            skLineSegment(sketch, "E107.6.44", {"start": v(0.79, -4.34) * mm, "end": v(0.83, -4.42) * mm});
            skLineSegment(sketch, "E107.6.45", {"start": v(0.18, -3.93) * mm, "end": v(0.28, -3.95) * mm});
            skLineSegment(sketch, "E107.6.46", {"start": v(0.28, -3.95) * mm, "end": v(0.36, -3.97) * mm});
            skLineSegment(sketch, "E107.6.47", {"start": v(0.36, -3.97) * mm, "end": v(0.44, -4) * mm});
            skLineSegment(sketch, "E107.6.48", {"start": v(0.44, -4) * mm, "end": v(0.5, -4.05) * mm});
            skLineSegment(sketch, "E107.6.49", {"start": v(0.5, -4.05) * mm, "end": v(0.57, -4.1) * mm});
            skLineSegment(sketch, "E107.6.50", {"start": v(0.57, -4.1) * mm, "end": v(0.63, -4.15) * mm});
            skLineSegment(sketch, "E107.6.51", {"start": v(0.63, -4.15) * mm, "end": v(0.69, -4.2) * mm});
            skLineSegment(sketch, "E107.6.52", {"start": v(-1.38, -5.94) * mm, "end": v(-1.44, -6.02) * mm});
            skLineSegment(sketch, "E107.6.53", {"start": v(1.82, -6.36) * mm, "end": v(1.9, -6.42) * mm});
            skLineSegment(sketch, "E107.6.54", {"start": v(-1.9, -6.42) * mm, "end": v(-2, -6.48) * mm});
            skLineSegment(sketch, "E107.6.55", {"start": v(-0.63, -4.15) * mm, "end": v(-0.69, -4.2) * mm});
            skLineSegment(sketch, "E107.6.56", {"start": v(0.83, -4.42) * mm, "end": v(0.87, -4.5) * mm});
            skLineSegment(sketch, "E107.6.57", {"start": v(-1.58, -6.16) * mm, "end": v(-1.66, -6.23) * mm});
            skLineSegment(sketch, "E107.6.58", {"start": v(1.31, -5.87) * mm, "end": v(1.38, -5.94) * mm});
            skLineSegment(sketch, "E107.6.59", {"start": v(1.9, -6.42) * mm, "end": v(2, -6.48) * mm});
            skLineSegment(sketch, "E107.6.60", {"start": v(0.99, -5.2) * mm, "end": v(0.99, -5.33) * mm});
            skLineSegment(sketch, "E107.6.61", {"start": v(-0.99, -5.2) * mm, "end": v(-0.99, -5.33) * mm});
            skLineSegment(sketch, "E107.6.62", {"start": v(-1.06, -5.49) * mm, "end": v(-1.1, -5.57) * mm});
            skLineSegment(sketch, "E107.6.63", {"start": v(0.87, -4.5) * mm, "end": v(0.9, -4.58) * mm});
            skLineSegment(sketch, "E107.6.64", {"start": v(-0.83, -4.42) * mm, "end": v(-0.87, -4.5) * mm});
            skLineSegment(sketch, "E107.6.65", {"start": v(1.38, -5.94) * mm, "end": v(1.44, -6.02) * mm});
            skLineSegment(sketch, "E107.6.66", {"start": v(-2, -6.48) * mm, "end": v(-2.08, -6.55) * mm});
            skLineSegment(sketch, "E107.6.67", {"start": v(2, -6.48) * mm, "end": v(2.08, -6.55) * mm});
            skLineSegment(sketch, "E107.6.68", {"start": v(0.99, -5.33) * mm, "end": v(1.02, -5.41) * mm});
            skLineSegment(sketch, "E107.6.69", {"start": v(-0.97, -4.87) * mm, "end": v(-0.99, -4.98) * mm});
            skLineSegment(sketch, "E107.6.70", {"start": v(-2.17, -6.6) * mm, "end": v(-2.27, -6.66) * mm});
            skLineSegment(sketch, "E107.6.71", {"start": v(0.9, -4.58) * mm, "end": v(0.93, -4.67) * mm});
            skLineSegment(sketch, "E107.6.72", {"start": v(-2.08, -6.55) * mm, "end": v(-2.17, -6.6) * mm});
            skLineSegment(sketch, "E107.6.73", {"start": v(-1.44, -6.02) * mm, "end": v(-1.51, -6.09) * mm});
            skLineSegment(sketch, "E107.6.74", {"start": v(1.44, -6.02) * mm, "end": v(1.51, -6.09) * mm});
            skLineSegment(sketch, "E107.6.75", {"start": v(-0.99, -5.33) * mm, "end": v(-1.02, -5.41) * mm});
            skLineSegment(sketch, "E107.6.76", {"start": v(0.97, -4.87) * mm, "end": v(0.99, -4.98) * mm});
            skLineSegment(sketch, "E107.6.77", {"start": v(0.99, -4.98) * mm, "end": v(1, -5.1) * mm});
            skLineSegment(sketch, "E107.6.78", {"start": v(1, -5.1) * mm, "end": v(0.99, -5.2) * mm});
            skLineSegment(sketch, "E107.6.79", {"start": v(2.66, -6.61) * mm, "end": v(2.73, -6.58) * mm});
            skLineSegment(sketch, "E107.6.80", {"start": v(-2.44, -6.7) * mm, "end": v(-2.51, -6.67) * mm});
            skLineSegment(sketch, "E107.6.81", {"start": v(-2.58, -6.64) * mm, "end": v(-2.66, -6.61) * mm});
            skLineSegment(sketch, "E107.6.82", {"start": v(-2.51, -6.67) * mm, "end": v(-2.58, -6.64) * mm});
            skLineSegment(sketch, "E107.6.83", {"start": v(2.44, -6.7) * mm, "end": v(2.51, -6.67) * mm});
            skLineSegment(sketch, "E107.6.84", {"start": v(-2.37, -6.72) * mm, "end": v(-2.44, -6.7) * mm});
            skLineSegment(sketch, "E107.6.85", {"start": v(2.37, -6.72) * mm, "end": v(2.44, -6.7) * mm});
            skLineSegment(sketch, "E107.6.86", {"start": v(2.51, -6.67) * mm, "end": v(2.58, -6.64) * mm});
            skLineSegment(sketch, "E107.6.87", {"start": v(-0.18, -3.93) * mm, "end": v(-0.28, -3.95) * mm});
            skLineSegment(sketch, "E107.6.88", {"start": v(2.58, -6.64) * mm, "end": v(2.66, -6.61) * mm});
            skLineSegment(sketch, "E107.6.89", {"start": v(-0.28, -3.95) * mm, "end": v(-0.36, -3.97) * mm});
            skLineSegment(sketch, "E107.6.90", {"start": v(-0.06, -3.92) * mm, "end": v(-0.18, -3.93) * mm});
            skLineSegment(sketch, "E107.6.91", {"start": v(-0.03, -3.92) * mm, "end": v(-0.04, -3.92) * mm});
            skLineSegment(sketch, "E107.6.92", {"start": v(0.01, -3.92) * mm, "end": v(0.03, -3.92) * mm});
            skLineSegment(sketch, "E107.6.93", {"start": v(0.06, -3.92) * mm, "end": v(0.18, -3.93) * mm});
            skLineSegment(sketch, "E107.6.94", {"start": v(0.05, -3.92) * mm, "end": v(0.06, -3.92) * mm});
            skLineSegment(sketch, "E107.6.95", {"start": v(0.04, -3.92) * mm, "end": v(0.05, -3.92) * mm});
            skLineSegment(sketch, "E107.6.96", {"start": v(0.03, -3.92) * mm, "end": v(0.04, -3.92) * mm});
            skLineSegment(sketch, "E107.6.97", {"start": v(0, -3.92) * mm, "end": v(0.01, -3.92) * mm});
            skLineSegment(sketch, "E107.6.98", {"start": v(0, -3.92) * mm, "end": v(-0.01, -3.92) * mm});
            skLineSegment(sketch, "E107.6.99", {"start": v(-0.01, -3.92) * mm, "end": v(-0.03, -3.92) * mm});
            skLineSegment(sketch, "E107.6.100", {"start": v(-0.04, -3.92) * mm, "end": v(-0.05, -3.92) * mm});
            skLineSegment(sketch, "E107.6.101", {"start": v(-0.05, -3.92) * mm, "end": v(-0.06, -3.92) * mm});
            skPoint(sketch, "E107.7.0", {"position": v(4.03, -4.03) * mm});
            skPoint(sketch, "E107.7.1", {"position": v(4.03, -4.03) * mm});
            skLineSegment(sketch, "E107.7.2", {"start": v(2.82, -4.22) * mm, "end": v(2.9, -4.3) * mm});
            skLineSegment(sketch, "E107.7.3", {"start": v(3.23, -5.58) * mm, "end": v(3.22, -5.68) * mm});
            skLineSegment(sketch, "E107.7.4", {"start": v(3.23, -5.37) * mm, "end": v(3.23, -5.47) * mm});
            skLineSegment(sketch, "E107.7.5", {"start": v(6.1, -3.16) * mm, "end": v(6.2, -3.13) * mm});
            skLineSegment(sketch, "E107.7.6", {"start": v(4.54, -3.1) * mm, "end": v(4.63, -3.14) * mm});
            skLineSegment(sketch, "E107.7.7", {"start": v(3.2, -5.78) * mm, "end": v(3.2, -5.89) * mm});
            skLineSegment(sketch, "E107.7.8", {"start": v(3.96, -2.65) * mm, "end": v(4.05, -2.7) * mm});
            skLineSegment(sketch, "E107.7.9", {"start": v(2.56, -3.06) * mm, "end": v(2.52, -3.15) * mm});
            skLineSegment(sketch, "E107.7.10", {"start": v(3.18, -4.8) * mm, "end": v(3.2, -4.9) * mm});
            skLineSegment(sketch, "E107.7.11", {"start": v(5.37, -3.23) * mm, "end": v(5.47, -3.23) * mm});
            skLineSegment(sketch, "E107.7.12", {"start": v(6.32, -3.1) * mm, "end": v(6.43, -3.08) * mm});
            skLineSegment(sketch, "E107.7.13", {"start": v(2.49, -3.46) * mm, "end": v(2.5, -3.54) * mm});
            skLineSegment(sketch, "E107.7.14", {"start": v(4.71, -3.16) * mm, "end": v(4.8, -3.18) * mm});
            skLineSegment(sketch, "E107.7.15", {"start": v(2.7, -4.05) * mm, "end": v(2.76, -4.13) * mm});
            skLineSegment(sketch, "E107.7.16", {"start": v(2.6, -3.88) * mm, "end": v(2.65, -3.96) * mm});
            skLineSegment(sketch, "E107.7.17", {"start": v(3.1, -4.54) * mm, "end": v(3.14, -4.63) * mm});
            skLineSegment(sketch, "E107.7.18", {"start": v(2.51, -3.63) * mm, "end": v(2.54, -3.71) * mm});
            skLineSegment(sketch, "E107.7.19", {"start": v(3.1, -6.32) * mm, "end": v(3.08, -6.43) * mm});
            skLineSegment(sketch, "E107.7.20", {"start": v(2.5, -3.22) * mm, "end": v(2.5, -3.3) * mm});
            skLineSegment(sketch, "E107.7.21", {"start": v(5.58, -3.23) * mm, "end": v(5.68, -3.22) * mm});
            skLineSegment(sketch, "E107.7.22", {"start": v(4.9, -3.2) * mm, "end": v(4.99, -3.21) * mm});
            skLineSegment(sketch, "E107.7.23", {"start": v(3.16, -4.71) * mm, "end": v(3.18, -4.8) * mm});
            skLineSegment(sketch, "E107.7.24", {"start": v(2.65, -3.96) * mm, "end": v(2.7, -4.05) * mm});
            skLineSegment(sketch, "E107.7.25", {"start": v(6.2, -3.13) * mm, "end": v(6.32, -3.1) * mm});
            skLineSegment(sketch, "E107.7.26", {"start": v(3.2, -4.9) * mm, "end": v(3.21, -4.99) * mm});
            skLineSegment(sketch, "E107.7.27", {"start": v(4.63, -3.14) * mm, "end": v(4.71, -3.16) * mm});
            skLineSegment(sketch, "E107.7.28", {"start": v(4.05, -2.7) * mm, "end": v(4.13, -2.76) * mm});
            skLineSegment(sketch, "E107.7.29", {"start": v(2.9, -4.3) * mm, "end": v(2.98, -4.38) * mm});
            skLineSegment(sketch, "E107.7.30", {"start": v(3.22, -5.08) * mm, "end": v(3.23, -5.18) * mm});
            skLineSegment(sketch, "E107.7.31", {"start": v(3.22, -5.68) * mm, "end": v(3.2, -5.78) * mm});
            skLineSegment(sketch, "E107.7.32", {"start": v(2.57, -3.8) * mm, "end": v(2.6, -3.88) * mm});
            skLineSegment(sketch, "E107.7.33", {"start": v(2.52, -3.15) * mm, "end": v(2.5, -3.22) * mm});
            skLineSegment(sketch, "E107.7.34", {"start": v(2.5, -3.54) * mm, "end": v(2.51, -3.63) * mm});
            skLineSegment(sketch, "E107.7.35", {"start": v(5.47, -3.23) * mm, "end": v(5.58, -3.23) * mm});
            skLineSegment(sketch, "E107.7.36", {"start": v(4.8, -3.18) * mm, "end": v(4.9, -3.2) * mm});
            skLineSegment(sketch, "E107.7.37", {"start": v(2.5, -3.3) * mm, "end": v(2.49, -3.38) * mm});
            skLineSegment(sketch, "E107.7.38", {"start": v(5.68, -3.22) * mm, "end": v(5.78, -3.2) * mm});
            skLineSegment(sketch, "E107.7.39", {"start": v(4.99, -3.21) * mm, "end": v(5.08, -3.22) * mm});
            skLineSegment(sketch, "E107.7.40", {"start": v(3.21, -4.99) * mm, "end": v(3.22, -5.08) * mm});
            skLineSegment(sketch, "E107.7.41", {"start": v(2.8, -6.55) * mm, "end": v(2.73, -6.58) * mm});
            skLineSegment(sketch, "E107.7.42", {"start": v(3.46, -2.49) * mm, "end": v(3.54, -2.5) * mm});
            skLineSegment(sketch, "E107.7.43", {"start": v(3.54, -2.5) * mm, "end": v(3.63, -2.51) * mm});
            skLineSegment(sketch, "E107.7.44", {"start": v(3.63, -2.51) * mm, "end": v(3.71, -2.54) * mm});
            skLineSegment(sketch, "E107.7.45", {"start": v(2.9, -2.65) * mm, "end": v(2.99, -2.6) * mm});
            skLineSegment(sketch, "E107.7.46", {"start": v(2.99, -2.6) * mm, "end": v(3.06, -2.56) * mm});
            skLineSegment(sketch, "E107.7.47", {"start": v(3.06, -2.56) * mm, "end": v(3.15, -2.52) * mm});
            skLineSegment(sketch, "E107.7.48", {"start": v(3.15, -2.52) * mm, "end": v(3.22, -2.5) * mm});
            skLineSegment(sketch, "E107.7.49", {"start": v(3.22, -2.5) * mm, "end": v(3.3, -2.5) * mm});
            skLineSegment(sketch, "E107.7.50", {"start": v(3.3, -2.5) * mm, "end": v(3.38, -2.49) * mm});
            skLineSegment(sketch, "E107.7.51", {"start": v(3.38, -2.49) * mm, "end": v(3.46, -2.49) * mm});
            skLineSegment(sketch, "E107.7.52", {"start": v(3.23, -5.18) * mm, "end": v(3.23, -5.27) * mm});
            skLineSegment(sketch, "E107.7.53", {"start": v(5.78, -3.2) * mm, "end": v(5.89, -3.2) * mm});
            skLineSegment(sketch, "E107.7.54", {"start": v(3.2, -5.89) * mm, "end": v(3.18, -6) * mm});
            skLineSegment(sketch, "E107.7.55", {"start": v(2.49, -3.38) * mm, "end": v(2.49, -3.46) * mm});
            skLineSegment(sketch, "E107.7.56", {"start": v(3.71, -2.54) * mm, "end": v(3.8, -2.57) * mm});
            skLineSegment(sketch, "E107.7.57", {"start": v(3.23, -5.47) * mm, "end": v(3.23, -5.58) * mm});
            skLineSegment(sketch, "E107.7.58", {"start": v(5.08, -3.22) * mm, "end": v(5.18, -3.23) * mm});
            skLineSegment(sketch, "E107.7.59", {"start": v(5.89, -3.2) * mm, "end": v(6, -3.18) * mm});
            skLineSegment(sketch, "E107.7.60", {"start": v(4.38, -2.98) * mm, "end": v(4.47, -3.07) * mm});
            skLineSegment(sketch, "E107.7.61", {"start": v(2.98, -4.38) * mm, "end": v(3.07, -4.47) * mm});
            skLineSegment(sketch, "E107.7.62", {"start": v(3.14, -4.63) * mm, "end": v(3.16, -4.71) * mm});
            skLineSegment(sketch, "E107.7.63", {"start": v(3.8, -2.57) * mm, "end": v(3.88, -2.6) * mm});
            skLineSegment(sketch, "E107.7.64", {"start": v(2.54, -3.71) * mm, "end": v(2.57, -3.8) * mm});
            skLineSegment(sketch, "E107.7.65", {"start": v(5.18, -3.23) * mm, "end": v(5.27, -3.23) * mm});
            skLineSegment(sketch, "E107.7.66", {"start": v(3.18, -6) * mm, "end": v(3.16, -6.1) * mm});
            skLineSegment(sketch, "E107.7.67", {"start": v(6, -3.18) * mm, "end": v(6.1, -3.16) * mm});
            skLineSegment(sketch, "E107.7.68", {"start": v(4.47, -3.07) * mm, "end": v(4.54, -3.1) * mm});
            skLineSegment(sketch, "E107.7.69", {"start": v(2.76, -4.13) * mm, "end": v(2.82, -4.22) * mm});
            skLineSegment(sketch, "E107.7.70", {"start": v(3.13, -6.2) * mm, "end": v(3.1, -6.32) * mm});
            skLineSegment(sketch, "E107.7.71", {"start": v(3.88, -2.6) * mm, "end": v(3.96, -2.65) * mm});
            skLineSegment(sketch, "E107.7.72", {"start": v(3.16, -6.1) * mm, "end": v(3.13, -6.2) * mm});
            skLineSegment(sketch, "E107.7.73", {"start": v(3.23, -5.27) * mm, "end": v(3.23, -5.37) * mm});
            skLineSegment(sketch, "E107.7.74", {"start": v(5.27, -3.23) * mm, "end": v(5.37, -3.23) * mm});
            skLineSegment(sketch, "E107.7.75", {"start": v(3.07, -4.47) * mm, "end": v(3.1, -4.54) * mm});
            skLineSegment(sketch, "E107.7.76", {"start": v(4.13, -2.76) * mm, "end": v(4.22, -2.82) * mm});
            skLineSegment(sketch, "E107.7.77", {"start": v(4.22, -2.82) * mm, "end": v(4.3, -2.9) * mm});
            skLineSegment(sketch, "E107.7.78", {"start": v(4.3, -2.9) * mm, "end": v(4.38, -2.98) * mm});
            skLineSegment(sketch, "E107.7.79", {"start": v(6.55, -2.8) * mm, "end": v(6.58, -2.73) * mm});
            skLineSegment(sketch, "E107.7.80", {"start": v(3, -6.46) * mm, "end": v(2.94, -6.5) * mm});
            skLineSegment(sketch, "E107.7.81", {"start": v(2.87, -6.52) * mm, "end": v(2.8, -6.55) * mm});
            skLineSegment(sketch, "E107.7.82", {"start": v(2.94, -6.5) * mm, "end": v(2.87, -6.52) * mm});
            skLineSegment(sketch, "E107.7.83", {"start": v(6.46, -3) * mm, "end": v(6.5, -2.94) * mm});
            skLineSegment(sketch, "E107.7.84", {"start": v(3.08, -6.43) * mm, "end": v(3, -6.46) * mm});
            skLineSegment(sketch, "E107.7.85", {"start": v(6.43, -3.08) * mm, "end": v(6.46, -3) * mm});
            skLineSegment(sketch, "E107.7.86", {"start": v(6.5, -2.94) * mm, "end": v(6.52, -2.87) * mm});
            skLineSegment(sketch, "E107.7.87", {"start": v(2.65, -2.9) * mm, "end": v(2.6, -2.99) * mm});
            skLineSegment(sketch, "E107.7.88", {"start": v(6.52, -2.87) * mm, "end": v(6.55, -2.8) * mm});
            skLineSegment(sketch, "E107.7.89", {"start": v(2.6, -2.99) * mm, "end": v(2.56, -3.06) * mm});
            skLineSegment(sketch, "E107.7.90", {"start": v(2.73, -2.82) * mm, "end": v(2.65, -2.9) * mm});
            skLineSegment(sketch, "E107.7.91", {"start": v(2.75, -2.79) * mm, "end": v(2.74, -2.8) * mm});
            skLineSegment(sketch, "E107.7.92", {"start": v(2.78, -2.76) * mm, "end": v(2.79, -2.75) * mm});
            skLineSegment(sketch, "E107.7.93", {"start": v(2.82, -2.73) * mm, "end": v(2.9, -2.65) * mm});
            skLineSegment(sketch, "E107.7.94", {"start": v(2.8, -2.74) * mm, "end": v(2.82, -2.73) * mm});
            skLineSegment(sketch, "E107.7.95", {"start": v(2.8, -2.74) * mm, "end": v(2.8, -2.74) * mm});
            skLineSegment(sketch, "E107.7.96", {"start": v(2.79, -2.75) * mm, "end": v(2.8, -2.74) * mm});
            skLineSegment(sketch, "E107.7.97", {"start": v(2.77, -2.77) * mm, "end": v(2.78, -2.76) * mm});
            skLineSegment(sketch, "E107.7.98", {"start": v(2.77, -2.77) * mm, "end": v(2.76, -2.78) * mm});
            skLineSegment(sketch, "E107.7.99", {"start": v(2.76, -2.78) * mm, "end": v(2.75, -2.79) * mm});
            skLineSegment(sketch, "E107.7.100", {"start": v(2.74, -2.8) * mm, "end": v(2.74, -2.8) * mm});
            skLineSegment(sketch, "E107.7.101", {"start": v(2.74, -2.8) * mm, "end": v(2.73, -2.82) * mm});
            skArc(sketch, "E108", {"start": v(-1.5, -1.32) * mm, "mid": v(2, 0) * mm, "end": v(-1.5, 1.32) * mm});
            skLineSegment(sketch, "E109", {"start": v(-1.5, 1.32) * mm, "end": v(-1.5, -1.32) * mm});
            skSolve(sketch);
        }
        {
            var Q0;
            Q0=makeQuery(id+"F0.imprint","IMPRINT",FACE,{"disambiguationData":[TD([[makeQuery(id+"F0.imprint","IMPRINT",EDGE,{"derivedFrom":sQuery(id+"F0.wireOp",EDGE,"E0")}),1.0]])]});
            extrude(context, id + "F1", {"entities" : qUnion([Q0]), "depth" : 3 * mm});
        }
    });
